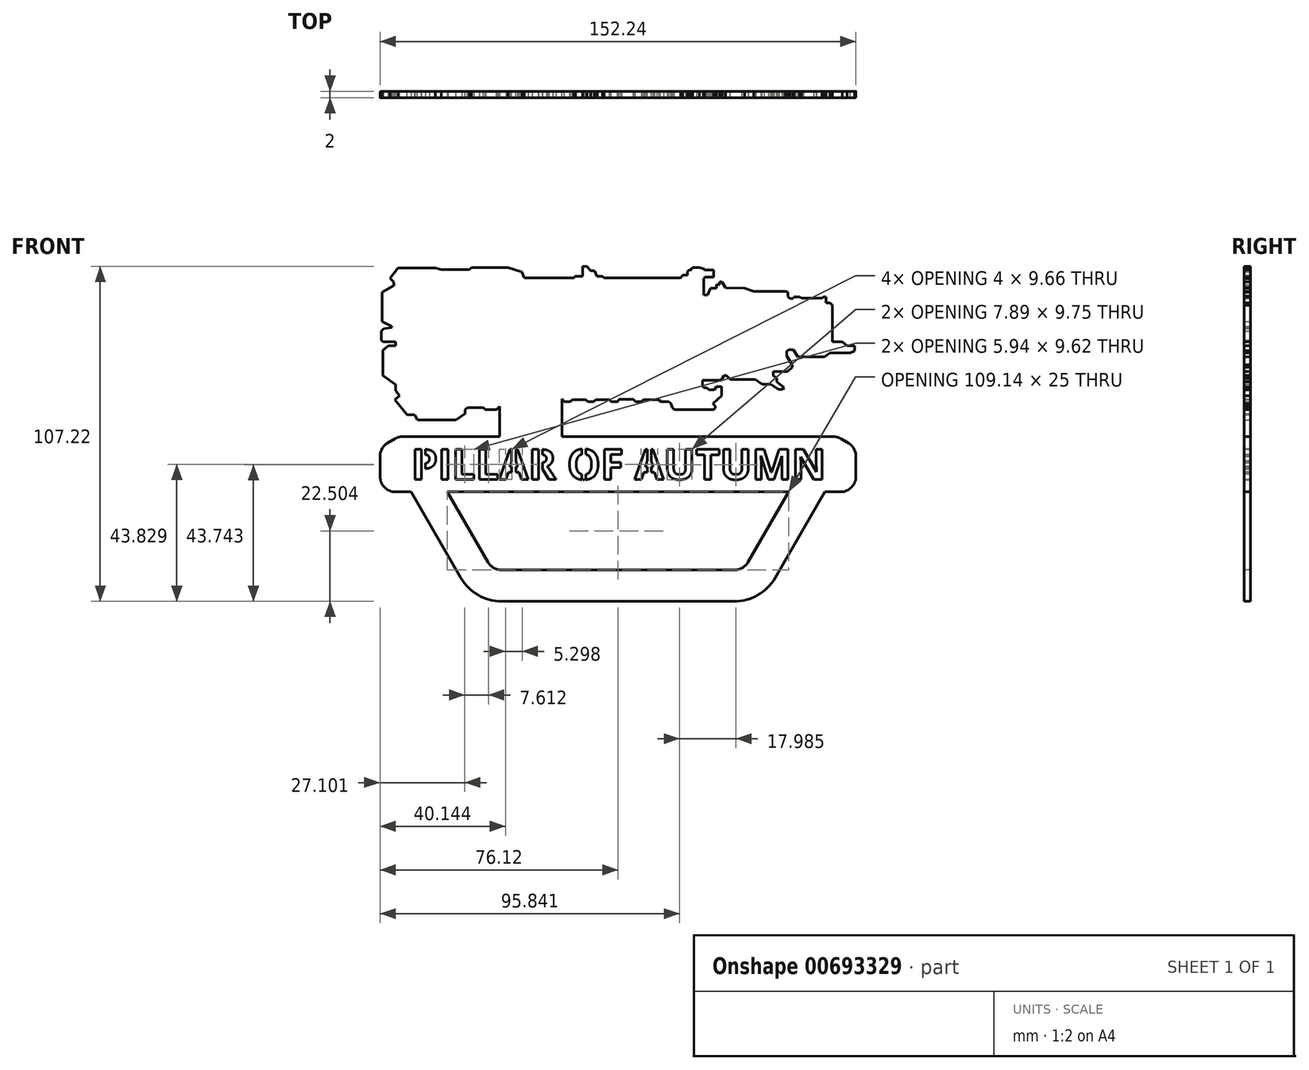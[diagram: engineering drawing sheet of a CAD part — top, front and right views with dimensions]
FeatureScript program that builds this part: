
annotation { "Feature Type Name" : "Feature", "Feature Type Description" : "" }
export const myFeature = defineFeature(function(context is Context, id is Id, definition is map)
    precondition{}
    {
        {
            var Q0;
            Q0=qCreatedBy(makeId("Front.planeOp"),FACE);
            var sketch = newSketch(context, id + "F0", { "sketchPlane" : qUnion([Q0])});
            skLineSegment(sketch, "E0", {"start": v(-54.7, 20.46) * mm, "end": v(-44.83, 20.46) * mm});
            skLineSegment(sketch, "E1", {"start": v(-44.83, 20.46) * mm, "end": v(-43.33, 20.02) * mm});
            skLineSegment(sketch, "E2", {"start": v(-43.33, 20.02) * mm, "end": v(-35.89, 20.02) * mm});
            skLineSegment(sketch, "E3", {"start": v(-35.89, 20.02) * mm, "end": v(-35.36, 20.5) * mm});
            skLineSegment(sketch, "E4", {"start": v(-35.36, 20.5) * mm, "end": v(-25.77, 20.5) * mm});
            skLineSegment(sketch, "E5", {"start": v(-25.77, 20.5) * mm, "end": v(-22.18, 19.35) * mm});
            skLineSegment(sketch, "E6", {"start": v(-22.18, 19.35) * mm, "end": v(-21.5, 17.82) * mm});
            skLineSegment(sketch, "E7", {"start": v(-21.5, 17.82) * mm, "end": v(-8.55, 17.82) * mm});
            skLineSegment(sketch, "E8", {"start": v(-8.55, 17.82) * mm, "end": v(-8.23, 18.3) * mm});
            skLineSegment(sketch, "E9", {"start": v(-8.23, 18.3) * mm, "end": v(-6.22, 18.3) * mm});
            skLineSegment(sketch, "E10", {"start": v(-6.22, 18.3) * mm, "end": v(-6.22, 20.89) * mm});
            skLineSegment(sketch, "E11", {"start": v(-6.22, 20.89) * mm, "end": v(-5.15, 20.89) * mm});
            skLineSegment(sketch, "E12", {"start": v(-5.15, 20.89) * mm, "end": v(-4.2, 19.76) * mm});
            skLineSegment(sketch, "E13", {"start": v(-4.2, 19.76) * mm, "end": v(-3.13, 19.76) * mm});
            skLineSegment(sketch, "E14", {"start": v(-3.13, 19.76) * mm, "end": v(-2.5, 18.3) * mm});
            skLineSegment(sketch, "E15", {"start": v(-2.5, 18.3) * mm, "end": v(-1.08, 18.3) * mm});
            skLineSegment(sketch, "E16", {"start": v(-1.08, 18.3) * mm, "end": v(-0.64, 17.82) * mm});
            skLineSegment(sketch, "E17", {"start": v(-0.64, 17.82) * mm, "end": v(19.49, 17.82) * mm});
            skLineSegment(sketch, "E18", {"start": v(19.49, 17.82) * mm, "end": v(19.98, 18.57) * mm});
            skLineSegment(sketch, "E19", {"start": v(19.98, 18.57) * mm, "end": v(21.22, 18.57) * mm});
            skLineSegment(sketch, "E20", {"start": v(21.22, 18.57) * mm, "end": v(21.22, 19.5) * mm});
            skLineSegment(sketch, "E21", {"start": v(21.22, 19.5) * mm, "end": v(21.62, 19.92) * mm});
            skLineSegment(sketch, "E22", {"start": v(21.62, 19.92) * mm, "end": v(22.31, 19.92) * mm});
            skLineSegment(sketch, "E23", {"start": v(22.31, 19.92) * mm, "end": v(22.31, 20.34) * mm});
            skLineSegment(sketch, "E24", {"start": v(22.31, 20.34) * mm, "end": v(22.56, 20.59) * mm});
            skLineSegment(sketch, "E25", {"start": v(22.56, 20.59) * mm, "end": v(24.39, 20.59) * mm});
            skLineSegment(sketch, "E26", {"start": v(24.39, 20.59) * mm, "end": v(25.46, 20.2) * mm});
            skLineSegment(sketch, "E27", {"start": v(25.46, 20.2) * mm, "end": v(25.7, 19.92) * mm});
            skLineSegment(sketch, "E28", {"start": v(25.7, 19.92) * mm, "end": v(28.13, 19.92) * mm});
            skLineSegment(sketch, "E29", {"start": v(28.13, 19.92) * mm, "end": v(28.13, 18.01) * mm});
            skLineSegment(sketch, "E30", {"start": v(28.13, 18.01) * mm, "end": v(25.76, 18.01) * mm});
            skLineSegment(sketch, "E31", {"start": v(25.76, 18.01) * mm, "end": v(25.46, 17.63) * mm});
            skLineSegment(sketch, "E32", {"start": v(25.46, 17.63) * mm, "end": v(25.46, 13.38) * mm});
            skLineSegment(sketch, "E33", {"start": v(25.46, 13.38) * mm, "end": v(26.57, 13.38) * mm});
            skLineSegment(sketch, "E34", {"start": v(26.57, 13.38) * mm, "end": v(27.23, 15.17) * mm});
            skLineSegment(sketch, "E35", {"start": v(27.23, 15.17) * mm, "end": v(28.85, 15.17) * mm});
            skLineSegment(sketch, "E36", {"start": v(28.85, 15.17) * mm, "end": v(28.85, 16.09) * mm});
            skLineSegment(sketch, "E37", {"start": v(28.85, 16.09) * mm, "end": v(29.71, 16.09) * mm});
            skLineSegment(sketch, "E38", {"start": v(29.71, 16.09) * mm, "end": v(29.71, 16.78) * mm});
            skLineSegment(sketch, "E39", {"start": v(29.71, 16.78) * mm, "end": v(30.29, 16.78) * mm});
            skLineSegment(sketch, "E40", {"start": v(30.29, 16.78) * mm, "end": v(31.21, 15.2) * mm});
            skLineSegment(sketch, "E41", {"start": v(31.21, 15.2) * mm, "end": v(36.22, 15.17) * mm});
            skLineSegment(sketch, "E42", {"start": v(36.22, 15.17) * mm, "end": v(38.62, 14.3) * mm});
            skLineSegment(sketch, "E43", {"start": v(38.62, 14.3) * mm, "end": v(46.94, 14.3) * mm});
            skLineSegment(sketch, "E44", {"start": v(46.94, 14.3) * mm, "end": v(47.62, 14.06) * mm});
            skLineSegment(sketch, "E45", {"start": v(47.62, 14.06) * mm, "end": v(47.62, 13) * mm});
            skLineSegment(sketch, "E46", {"start": v(47.62, 13) * mm, "end": v(48.07, 12.38) * mm});
            skLineSegment(sketch, "E47", {"start": v(48.07, 12.38) * mm, "end": v(48.92, 12.38) * mm});
            skLineSegment(sketch, "E48", {"start": v(48.92, 12.38) * mm, "end": v(49.1, 12.88) * mm});
            skLineSegment(sketch, "E49", {"start": v(49.1, 12.88) * mm, "end": v(50.74, 12.88) * mm});
            skLineSegment(sketch, "E50", {"start": v(50.74, 12.88) * mm, "end": v(51.11, 12.5) * mm});
            skLineSegment(sketch, "E51", {"start": v(51.11, 12.5) * mm, "end": v(56.53, 12.5) * mm});
            skLineSegment(sketch, "E52", {"start": v(56.53, 12.5) * mm, "end": v(56.87, 12.88) * mm});
            skLineSegment(sketch, "E53", {"start": v(56.87, 12.88) * mm, "end": v(57.58, 12.88) * mm});
            skLineSegment(sketch, "E54", {"start": v(57.58, 12.88) * mm, "end": v(57.58, 11.32) * mm});
            skLineSegment(sketch, "E55", {"start": v(57.58, 11.32) * mm, "end": v(58.55, 11.32) * mm});
            skLineSegment(sketch, "E56", {"start": v(58.55, 11.32) * mm, "end": v(59.24, 10.67) * mm});
            skLineSegment(sketch, "E57", {"start": v(59.24, 10.67) * mm, "end": v(59.24, 1.08) * mm});
            skLineSegment(sketch, "E58", {"start": v(59.24, 1.08) * mm, "end": v(61.8, 1.08) * mm});
            skLineSegment(sketch, "E59", {"start": v(61.8, 1.08) * mm, "end": v(63.08, 0) * mm});
            skLineSegment(sketch, "E60", {"start": v(63.08, 0) * mm, "end": v(65.04, 0) * mm});
            skLineSegment(sketch, "E61", {"start": v(65.04, 0) * mm, "end": v(65.04, -1.34) * mm});
            skLineSegment(sketch, "E62", {"start": v(65.04, -1.34) * mm, "end": v(63.94, -1.8) * mm});
            skLineSegment(sketch, "E63", {"start": v(63.94, -1.8) * mm, "end": v(58.55, -1.8) * mm});
            skLineSegment(sketch, "E64", {"start": v(58.55, -1.8) * mm, "end": v(57.14, -2.9) * mm});
            skLineSegment(sketch, "E65", {"start": v(57.14, -2.9) * mm, "end": v(50.16, -2.9) * mm});
            skLineSegment(sketch, "E66", {"start": v(50.16, -2.9) * mm, "end": v(49.07, -1.06) * mm});
            skLineSegment(sketch, "E67", {"start": v(49.07, -1.06) * mm, "end": v(47.74, -1.06) * mm});
            skLineSegment(sketch, "E68", {"start": v(47.74, -1.06) * mm, "end": v(47.27, -1.4) * mm});
            skLineSegment(sketch, "E69", {"start": v(47.27, -1.4) * mm, "end": v(47.27, -2.63) * mm});
            skLineSegment(sketch, "E70", {"start": v(47.27, -2.63) * mm, "end": v(48.68, -5) * mm});
            skLineSegment(sketch, "E71", {"start": v(48.68, -5) * mm, "end": v(48.68, -5.57) * mm});
            skLineSegment(sketch, "E72", {"start": v(48.68, -5.57) * mm, "end": v(47.41, -6.74) * mm});
            skLineSegment(sketch, "E73", {"start": v(47.41, -6.74) * mm, "end": v(43.7, -6.74) * mm});
            skLineSegment(sketch, "E74", {"start": v(43.7, -6.74) * mm, "end": v(43.7, -7.74) * mm});
            skLineSegment(sketch, "E75", {"start": v(43.7, -7.74) * mm, "end": v(44.62, -8.55) * mm});
            skLineSegment(sketch, "E76", {"start": v(44.62, -8.55) * mm, "end": v(44.62, -9.42) * mm});
            skLineSegment(sketch, "E77", {"start": v(44.62, -9.42) * mm, "end": v(46.58, -10.94) * mm});
            skLineSegment(sketch, "E78", {"start": v(46.58, -10.94) * mm, "end": v(46.23, -11.38) * mm});
            skLineSegment(sketch, "E79", {"start": v(46.23, -11.38) * mm, "end": v(45.04, -11.38) * mm});
            skLineSegment(sketch, "E80", {"start": v(45.04, -11.38) * mm, "end": v(43.12, -10.02) * mm});
            skLineSegment(sketch, "E81", {"start": v(43.12, -10.02) * mm, "end": v(40.82, -10.02) * mm});
            skLineSegment(sketch, "E82", {"start": v(40.82, -10.02) * mm, "end": v(39.07, -8.83) * mm});
            skLineSegment(sketch, "E83", {"start": v(39.07, -8.83) * mm, "end": v(32.52, -8.83) * mm});
            skLineSegment(sketch, "E84", {"start": v(32.52, -8.83) * mm, "end": v(31.4, -7.8) * mm});
            skLineSegment(sketch, "E85", {"start": v(31.4, -7.8) * mm, "end": v(30.76, -7.8) * mm});
            skLineSegment(sketch, "E86", {"start": v(30.76, -7.8) * mm, "end": v(30.06, -9.02) * mm});
            skLineSegment(sketch, "E87", {"start": v(30.06, -9.02) * mm, "end": v(25.2, -9.02) * mm});
            skLineSegment(sketch, "E88", {"start": v(25.2, -9.02) * mm, "end": v(25.2, -10.62) * mm});
            skLineSegment(sketch, "E89", {"start": v(25.2, -10.62) * mm, "end": v(25.6, -11.03) * mm});
            skLineSegment(sketch, "E90", {"start": v(25.6, -11.03) * mm, "end": v(26.3, -11.03) * mm});
            skLineSegment(sketch, "E91", {"start": v(26.3, -11.03) * mm, "end": v(26.81, -11.57) * mm});
            skLineSegment(sketch, "E92", {"start": v(26.81, -11.57) * mm, "end": v(28.34, -11.57) * mm});
            skLineSegment(sketch, "E93", {"start": v(28.34, -11.57) * mm, "end": v(28.87, -10.67) * mm});
            skLineSegment(sketch, "E94", {"start": v(28.87, -10.67) * mm, "end": v(30.18, -10.67) * mm});
            skLineSegment(sketch, "E95", {"start": v(30.18, -10.67) * mm, "end": v(30.18, -13.07) * mm});
            skLineSegment(sketch, "E96", {"start": v(30.18, -13.07) * mm, "end": v(27.93, -15.14) * mm});
            skLineSegment(sketch, "E97", {"start": v(27.93, -15.14) * mm, "end": v(28.48, -15.74) * mm});
            skLineSegment(sketch, "E98", {"start": v(28.48, -15.74) * mm, "end": v(28.48, -16.3) * mm});
            skLineSegment(sketch, "E99", {"start": v(28.48, -16.3) * mm, "end": v(28.11, -16.7) * mm});
            skLineSegment(sketch, "E100", {"start": v(28.11, -16.7) * mm, "end": v(17.79, -16.7) * mm});
            skLineSegment(sketch, "E101", {"start": v(17.79, -16.7) * mm, "end": v(17.26, -16.2) * mm});
            skLineSegment(sketch, "E102", {"start": v(17.26, -16.2) * mm, "end": v(16.82, -15.01) * mm});
            skLineSegment(sketch, "E103", {"start": v(16.82, -15.01) * mm, "end": v(16.34, -14.6) * mm});
            skLineSegment(sketch, "E104", {"start": v(16.34, -14.6) * mm, "end": v(14.18, -14.67) * mm});
            skLineSegment(sketch, "E105", {"start": v(14.18, -14.67) * mm, "end": v(13.8, -14.17) * mm});
            skLineSegment(sketch, "E106", {"start": v(13.8, -14.17) * mm, "end": v(9.68, -14.17) * mm});
            skLineSegment(sketch, "E107", {"start": v(9.68, -14.17) * mm, "end": v(9.26, -14.68) * mm});
            skLineSegment(sketch, "E108", {"start": v(9.26, -14.68) * mm, "end": v(7.64, -14.68) * mm});
            skLineSegment(sketch, "E109", {"start": v(7.64, -14.68) * mm, "end": v(7.1, -14.07) * mm});
            skLineSegment(sketch, "E110", {"start": v(7.1, -14.07) * mm, "end": v(3.34, -14.07) * mm});
            skLineSegment(sketch, "E111", {"start": v(3.34, -14.07) * mm, "end": v(2.95, -14.65) * mm});
            skLineSegment(sketch, "E112", {"start": v(2.95, -14.65) * mm, "end": v(1.26, -14.65) * mm});
            skLineSegment(sketch, "E113", {"start": v(1.26, -14.65) * mm, "end": v(0.83, -14.1) * mm});
            skLineSegment(sketch, "E114", {"start": v(0.83, -14.1) * mm, "end": v(-2.8, -14.1) * mm});
            skLineSegment(sketch, "E115", {"start": v(-2.8, -14.1) * mm, "end": v(-3.29, -14.65) * mm});
            skLineSegment(sketch, "E116", {"start": v(-3.29, -14.65) * mm, "end": v(-4.88, -14.65) * mm});
            skLineSegment(sketch, "E117", {"start": v(-4.88, -14.65) * mm, "end": v(-5.47, -14.11) * mm});
            skLineSegment(sketch, "E118", {"start": v(-5.47, -14.11) * mm, "end": v(-9, -14.11) * mm});
            skLineSegment(sketch, "E119", {"start": v(-9, -14.11) * mm, "end": v(-9.5, -14.65) * mm});
            skLineSegment(sketch, "E120", {"start": v(-9.5, -14.65) * mm, "end": v(-11.05, -14.65) * mm});
            skLineSegment(sketch, "E121", {"start": v(-11.05, -14.65) * mm, "end": v(-11.63, -13.96) * mm});
            skLineSegment(sketch, "E122", {"start": v(-11.63, -13.96) * mm, "end": v(-14.05, -13.96) * mm});
            skLineSegment(sketch, "E123", {"start": v(-14.05, -13.96) * mm, "end": v(-16.32, -16.2) * mm});
            skLineSegment(sketch, "E124", {"start": v(-16.32, -16.2) * mm, "end": v(-25.86, -16.2) * mm});
            skLineSegment(sketch, "E125", {"start": v(-25.86, -16.2) * mm, "end": v(-26.54, -15.2) * mm});
            skLineSegment(sketch, "E126", {"start": v(-26.54, -15.2) * mm, "end": v(-27.3, -15.2) * mm});
            skLineSegment(sketch, "E127", {"start": v(-27.3, -15.2) * mm, "end": v(-28.87, -16.7) * mm});
            skLineSegment(sketch, "E128", {"start": v(-28.87, -16.7) * mm, "end": v(-31.79, -16.7) * mm});
            skLineSegment(sketch, "E129", {"start": v(-31.79, -16.7) * mm, "end": v(-32.27, -16.2) * mm});
            skLineSegment(sketch, "E130", {"start": v(-32.27, -16.2) * mm, "end": v(-36.4, -16.2) * mm});
            skLineSegment(sketch, "E131", {"start": v(-36.4, -16.2) * mm, "end": v(-37.06, -16.7) * mm});
            skLineSegment(sketch, "E132", {"start": v(-37.06, -16.7) * mm, "end": v(-37.06, -17.8) * mm});
            skLineSegment(sketch, "E133", {"start": v(-37.06, -17.8) * mm, "end": v(-39.5, -19.41) * mm});
            skLineSegment(sketch, "E134", {"start": v(-39.5, -19.41) * mm, "end": v(-49.57, -19.41) * mm});
            skLineSegment(sketch, "E135", {"start": v(-49.57, -19.41) * mm, "end": v(-50.32, -18.05) * mm});
            skLineSegment(sketch, "E136", {"start": v(-50.32, -18.05) * mm, "end": v(-52.28, -18.05) * mm});
            skLineSegment(sketch, "E137", {"start": v(-52.28, -18.05) * mm, "end": v(-55.5, -14.11) * mm});
            skLineSegment(sketch, "E138", {"start": v(-55.5, -14.11) * mm, "end": v(-54.23, -13.06) * mm});
            skLineSegment(sketch, "E139", {"start": v(-54.23, -13.06) * mm, "end": v(-55.3, -11.76) * mm});
            skLineSegment(sketch, "E140", {"start": v(-55.3, -11.76) * mm, "end": v(-55.3, -10.21) * mm});
            skLineSegment(sketch, "E141", {"start": v(-55.3, -10.21) * mm, "end": v(-58.58, -7.82) * mm});
            skLineSegment(sketch, "E142", {"start": v(-58.58, -7.82) * mm, "end": v(-58.58, -1.1) * mm});
            skLineSegment(sketch, "E143", {"start": v(-58.58, -1.1) * mm, "end": v(-57.2, 0) * mm});
            skLineSegment(sketch, "E144", {"start": v(-57.2, 0) * mm, "end": v(-55.3, 0) * mm});
            skLineSegment(sketch, "E145", {"start": v(-55.3, 0) * mm, "end": v(-55.3, 1.1) * mm});
            skLineSegment(sketch, "E146", {"start": v(-55.3, 1.1) * mm, "end": v(-58.58, 1.1) * mm});
            skLineSegment(sketch, "E147", {"start": v(-58.58, 1.1) * mm, "end": v(-59, 1.53) * mm});
            skLineSegment(sketch, "E148", {"start": v(-59, 1.53) * mm, "end": v(-59, 3.87) * mm});
            skLineSegment(sketch, "E149", {"start": v(-59, 3.87) * mm, "end": v(-58.42, 4.53) * mm});
            skLineSegment(sketch, "E150", {"start": v(-58.42, 4.53) * mm, "end": v(-56.24, 4.83) * mm});
            skLineSegment(sketch, "E151", {"start": v(-56.24, 4.83) * mm, "end": v(-56.28, 5.09) * mm});
            skLineSegment(sketch, "E152", {"start": v(-56.28, 5.09) * mm, "end": v(-58.86, 6.39) * mm});
            skLineSegment(sketch, "E153", {"start": v(-58.86, 6.39) * mm, "end": v(-58.86, 14.13) * mm});
            skLineSegment(sketch, "E154", {"start": v(-58.86, 14.13) * mm, "end": v(-55.69, 15.85) * mm});
            skLineSegment(sketch, "E155", {"start": v(-55.69, 15.85) * mm, "end": v(-55.81, 16.76) * mm});
            skLineSegment(sketch, "E156", {"start": v(-55.81, 16.76) * mm, "end": v(-56.75, 17.77) * mm});
            skLineSegment(sketch, "E157", {"start": v(-56.75, 17.77) * mm, "end": v(-54.7, 20.46) * mm});
            skSolve(sketch);
        }
        {
            var Q0;
            Q0 = qSketchRegion(id + "F0", true);
            extrude(context, id + "F1", {"entities" : qUnion([Q0]), "depth" : 2 * mm, "offsetDistance" : 25 * mm});
        }
        {
            var Q0;
            Q0=makeQuery(id+"F1.opExtrude","SWEPT_BODY",BODY,{"disambiguationData":[OSD([sQuery(id+"F0.wireOp",EDGE,"E0"),sQuery(id+"F0.wireOp",EDGE,"E1"),sQuery(id+"F0.wireOp",EDGE,"E2"),sQuery(id+"F0.wireOp",EDGE,"E3"),sQuery(id+"F0.wireOp",EDGE,"E4"),sQuery(id+"F0.wireOp",EDGE,"E5"),sQuery(id+"F0.wireOp",EDGE,"E6"),sQuery(id+"F0.wireOp",EDGE,"E7"),sQuery(id+"F0.wireOp",EDGE,"E8"),sQuery(id+"F0.wireOp",EDGE,"E9"),sQuery(id+"F0.wireOp",EDGE,"E10"),sQuery(id+"F0.wireOp",EDGE,"E11"),sQuery(id+"F0.wireOp",EDGE,"E12"),sQuery(id+"F0.wireOp",EDGE,"E13"),sQuery(id+"F0.wireOp",EDGE,"E14"),sQuery(id+"F0.wireOp",EDGE,"E15"),sQuery(id+"F0.wireOp",EDGE,"E16"),sQuery(id+"F0.wireOp",EDGE,"E17"),sQuery(id+"F0.wireOp",EDGE,"E18"),sQuery(id+"F0.wireOp",EDGE,"E19"),sQuery(id+"F0.wireOp",EDGE,"E20"),sQuery(id+"F0.wireOp",EDGE,"E21"),sQuery(id+"F0.wireOp",EDGE,"E22"),sQuery(id+"F0.wireOp",EDGE,"E23"),sQuery(id+"F0.wireOp",EDGE,"E24"),sQuery(id+"F0.wireOp",EDGE,"E25"),sQuery(id+"F0.wireOp",EDGE,"E26"),sQuery(id+"F0.wireOp",EDGE,"E27"),sQuery(id+"F0.wireOp",EDGE,"E28"),sQuery(id+"F0.wireOp",EDGE,"E29"),sQuery(id+"F0.wireOp",EDGE,"E30"),sQuery(id+"F0.wireOp",EDGE,"E31"),sQuery(id+"F0.wireOp",EDGE,"E32"),sQuery(id+"F0.wireOp",EDGE,"E33"),sQuery(id+"F0.wireOp",EDGE,"E34"),sQuery(id+"F0.wireOp",EDGE,"E35"),sQuery(id+"F0.wireOp",EDGE,"E36"),sQuery(id+"F0.wireOp",EDGE,"E37"),sQuery(id+"F0.wireOp",EDGE,"E38"),sQuery(id+"F0.wireOp",EDGE,"E39"),sQuery(id+"F0.wireOp",EDGE,"E40"),sQuery(id+"F0.wireOp",EDGE,"E41"),sQuery(id+"F0.wireOp",EDGE,"E42"),sQuery(id+"F0.wireOp",EDGE,"E43"),sQuery(id+"F0.wireOp",EDGE,"E44"),sQuery(id+"F0.wireOp",EDGE,"E45"),sQuery(id+"F0.wireOp",EDGE,"E46"),sQuery(id+"F0.wireOp",EDGE,"E47"),sQuery(id+"F0.wireOp",EDGE,"E48"),sQuery(id+"F0.wireOp",EDGE,"E49"),sQuery(id+"F0.wireOp",EDGE,"E50"),sQuery(id+"F0.wireOp",EDGE,"E51"),sQuery(id+"F0.wireOp",EDGE,"E52"),sQuery(id+"F0.wireOp",EDGE,"E53"),sQuery(id+"F0.wireOp",EDGE,"E54"),sQuery(id+"F0.wireOp",EDGE,"E55"),sQuery(id+"F0.wireOp",EDGE,"E56"),sQuery(id+"F0.wireOp",EDGE,"E57"),sQuery(id+"F0.wireOp",EDGE,"E58"),sQuery(id+"F0.wireOp",EDGE,"E59"),sQuery(id+"F0.wireOp",EDGE,"E60"),sQuery(id+"F0.wireOp",EDGE,"E61"),sQuery(id+"F0.wireOp",EDGE,"E62"),sQuery(id+"F0.wireOp",EDGE,"E63"),sQuery(id+"F0.wireOp",EDGE,"E64"),sQuery(id+"F0.wireOp",EDGE,"E65"),sQuery(id+"F0.wireOp",EDGE,"E66"),sQuery(id+"F0.wireOp",EDGE,"E67"),sQuery(id+"F0.wireOp",EDGE,"E68"),sQuery(id+"F0.wireOp",EDGE,"E69"),sQuery(id+"F0.wireOp",EDGE,"E70"),sQuery(id+"F0.wireOp",EDGE,"E71"),sQuery(id+"F0.wireOp",EDGE,"E72"),sQuery(id+"F0.wireOp",EDGE,"E73"),sQuery(id+"F0.wireOp",EDGE,"E74"),sQuery(id+"F0.wireOp",EDGE,"E75"),sQuery(id+"F0.wireOp",EDGE,"E76"),sQuery(id+"F0.wireOp",EDGE,"E77"),sQuery(id+"F0.wireOp",EDGE,"E78"),sQuery(id+"F0.wireOp",EDGE,"E79"),sQuery(id+"F0.wireOp",EDGE,"E80"),sQuery(id+"F0.wireOp",EDGE,"E81"),sQuery(id+"F0.wireOp",EDGE,"E82"),sQuery(id+"F0.wireOp",EDGE,"E83"),sQuery(id+"F0.wireOp",EDGE,"E84"),sQuery(id+"F0.wireOp",EDGE,"E85"),sQuery(id+"F0.wireOp",EDGE,"E86"),sQuery(id+"F0.wireOp",EDGE,"E87"),sQuery(id+"F0.wireOp",EDGE,"E88"),sQuery(id+"F0.wireOp",EDGE,"E89"),sQuery(id+"F0.wireOp",EDGE,"E90"),sQuery(id+"F0.wireOp",EDGE,"E91"),sQuery(id+"F0.wireOp",EDGE,"E92"),sQuery(id+"F0.wireOp",EDGE,"E93"),sQuery(id+"F0.wireOp",EDGE,"E94"),sQuery(id+"F0.wireOp",EDGE,"E95"),sQuery(id+"F0.wireOp",EDGE,"E96"),sQuery(id+"F0.wireOp",EDGE,"E97"),sQuery(id+"F0.wireOp",EDGE,"E98"),sQuery(id+"F0.wireOp",EDGE,"E99"),sQuery(id+"F0.wireOp",EDGE,"E100"),sQuery(id+"F0.wireOp",EDGE,"E101"),sQuery(id+"F0.wireOp",EDGE,"E102"),sQuery(id+"F0.wireOp",EDGE,"E103"),sQuery(id+"F0.wireOp",EDGE,"E104"),sQuery(id+"F0.wireOp",EDGE,"E105"),sQuery(id+"F0.wireOp",EDGE,"E106"),sQuery(id+"F0.wireOp",EDGE,"E107"),sQuery(id+"F0.wireOp",EDGE,"E108"),sQuery(id+"F0.wireOp",EDGE,"E109"),sQuery(id+"F0.wireOp",EDGE,"E110"),sQuery(id+"F0.wireOp",EDGE,"E111"),sQuery(id+"F0.wireOp",EDGE,"E112"),sQuery(id+"F0.wireOp",EDGE,"E113"),sQuery(id+"F0.wireOp",EDGE,"E114"),sQuery(id+"F0.wireOp",EDGE,"E115"),sQuery(id+"F0.wireOp",EDGE,"E116"),sQuery(id+"F0.wireOp",EDGE,"E117"),sQuery(id+"F0.wireOp",EDGE,"E118"),sQuery(id+"F0.wireOp",EDGE,"E119"),sQuery(id+"F0.wireOp",EDGE,"E120"),sQuery(id+"F0.wireOp",EDGE,"E121"),sQuery(id+"F0.wireOp",EDGE,"E122"),sQuery(id+"F0.wireOp",EDGE,"E123"),sQuery(id+"F0.wireOp",EDGE,"E124"),sQuery(id+"F0.wireOp",EDGE,"E125"),sQuery(id+"F0.wireOp",EDGE,"E126"),sQuery(id+"F0.wireOp",EDGE,"E127"),sQuery(id+"F0.wireOp",EDGE,"E128"),sQuery(id+"F0.wireOp",EDGE,"E129"),sQuery(id+"F0.wireOp",EDGE,"E130"),sQuery(id+"F0.wireOp",EDGE,"E131"),sQuery(id+"F0.wireOp",EDGE,"E132"),sQuery(id+"F0.wireOp",EDGE,"E133"),sQuery(id+"F0.wireOp",EDGE,"E134"),sQuery(id+"F0.wireOp",EDGE,"E135"),sQuery(id+"F0.wireOp",EDGE,"E136"),sQuery(id+"F0.wireOp",EDGE,"E137"),sQuery(id+"F0.wireOp",EDGE,"E138"),sQuery(id+"F0.wireOp",EDGE,"E139"),sQuery(id+"F0.wireOp",EDGE,"E140"),sQuery(id+"F0.wireOp",EDGE,"E141"),sQuery(id+"F0.wireOp",EDGE,"E142"),sQuery(id+"F0.wireOp",EDGE,"E143"),sQuery(id+"F0.wireOp",EDGE,"E144"),sQuery(id+"F0.wireOp",EDGE,"E145"),sQuery(id+"F0.wireOp",EDGE,"E146"),sQuery(id+"F0.wireOp",EDGE,"E147"),sQuery(id+"F0.wireOp",EDGE,"E148"),sQuery(id+"F0.wireOp",EDGE,"E149"),sQuery(id+"F0.wireOp",EDGE,"E150"),sQuery(id+"F0.wireOp",EDGE,"E151"),sQuery(id+"F0.wireOp",EDGE,"E152"),sQuery(id+"F0.wireOp",EDGE,"E153"),sQuery(id+"F0.wireOp",EDGE,"E154"),sQuery(id+"F0.wireOp",EDGE,"E155"),sQuery(id+"F0.wireOp",EDGE,"E156"),sQuery(id+"F0.wireOp",EDGE,"E157")])]});
            var Q1;
            Q1=makeQuery(id+"F1.opExtrude","CAP_VERTEX",VERTEX,{"disambiguationData":[OSD([sQuery(id+"F0.wireOp",EDGE,"E145"),sQuery(id+"F0.wireOp",EDGE,"E146")])],"isStart":false});
            transform(context, id + "F2", {"entities" : qUnion([Q0]), "transformType" : TransformType.SCALE_UNIFORMLY, "scale" : 1.22, "scalePoint" : qUnion([Q1]), "makeCopy" : false});
        }
        {
            var Q0;
            Q0=makeQuery(id+"F1.opExtrude","CAP_FACE",FACE,{"disambiguationData":[OSD([sQuery(id+"F0.wireOp",EDGE,"E0"),sQuery(id+"F0.wireOp",EDGE,"E1"),sQuery(id+"F0.wireOp",EDGE,"E2"),sQuery(id+"F0.wireOp",EDGE,"E3"),sQuery(id+"F0.wireOp",EDGE,"E4"),sQuery(id+"F0.wireOp",EDGE,"E5"),sQuery(id+"F0.wireOp",EDGE,"E6"),sQuery(id+"F0.wireOp",EDGE,"E7"),sQuery(id+"F0.wireOp",EDGE,"E8"),sQuery(id+"F0.wireOp",EDGE,"E9"),sQuery(id+"F0.wireOp",EDGE,"E10"),sQuery(id+"F0.wireOp",EDGE,"E11"),sQuery(id+"F0.wireOp",EDGE,"E12"),sQuery(id+"F0.wireOp",EDGE,"E13"),sQuery(id+"F0.wireOp",EDGE,"E14"),sQuery(id+"F0.wireOp",EDGE,"E15"),sQuery(id+"F0.wireOp",EDGE,"E16"),sQuery(id+"F0.wireOp",EDGE,"E17"),sQuery(id+"F0.wireOp",EDGE,"E18"),sQuery(id+"F0.wireOp",EDGE,"E19"),sQuery(id+"F0.wireOp",EDGE,"E20"),sQuery(id+"F0.wireOp",EDGE,"E21"),sQuery(id+"F0.wireOp",EDGE,"E22"),sQuery(id+"F0.wireOp",EDGE,"E23"),sQuery(id+"F0.wireOp",EDGE,"E24"),sQuery(id+"F0.wireOp",EDGE,"E25"),sQuery(id+"F0.wireOp",EDGE,"E26"),sQuery(id+"F0.wireOp",EDGE,"E27"),sQuery(id+"F0.wireOp",EDGE,"E28"),sQuery(id+"F0.wireOp",EDGE,"E29"),sQuery(id+"F0.wireOp",EDGE,"E30"),sQuery(id+"F0.wireOp",EDGE,"E31"),sQuery(id+"F0.wireOp",EDGE,"E32"),sQuery(id+"F0.wireOp",EDGE,"E33"),sQuery(id+"F0.wireOp",EDGE,"E34"),sQuery(id+"F0.wireOp",EDGE,"E35"),sQuery(id+"F0.wireOp",EDGE,"E36"),sQuery(id+"F0.wireOp",EDGE,"E37"),sQuery(id+"F0.wireOp",EDGE,"E38"),sQuery(id+"F0.wireOp",EDGE,"E39"),sQuery(id+"F0.wireOp",EDGE,"E40"),sQuery(id+"F0.wireOp",EDGE,"E41"),sQuery(id+"F0.wireOp",EDGE,"E42"),sQuery(id+"F0.wireOp",EDGE,"E43"),sQuery(id+"F0.wireOp",EDGE,"E44"),sQuery(id+"F0.wireOp",EDGE,"E45"),sQuery(id+"F0.wireOp",EDGE,"E46"),sQuery(id+"F0.wireOp",EDGE,"E47"),sQuery(id+"F0.wireOp",EDGE,"E48"),sQuery(id+"F0.wireOp",EDGE,"E49"),sQuery(id+"F0.wireOp",EDGE,"E50"),sQuery(id+"F0.wireOp",EDGE,"E51"),sQuery(id+"F0.wireOp",EDGE,"E52"),sQuery(id+"F0.wireOp",EDGE,"E53"),sQuery(id+"F0.wireOp",EDGE,"E54"),sQuery(id+"F0.wireOp",EDGE,"E55"),sQuery(id+"F0.wireOp",EDGE,"E56"),sQuery(id+"F0.wireOp",EDGE,"E57"),sQuery(id+"F0.wireOp",EDGE,"E58"),sQuery(id+"F0.wireOp",EDGE,"E59"),sQuery(id+"F0.wireOp",EDGE,"E60"),sQuery(id+"F0.wireOp",EDGE,"E61"),sQuery(id+"F0.wireOp",EDGE,"E62"),sQuery(id+"F0.wireOp",EDGE,"E63"),sQuery(id+"F0.wireOp",EDGE,"E64"),sQuery(id+"F0.wireOp",EDGE,"E65"),sQuery(id+"F0.wireOp",EDGE,"E66"),sQuery(id+"F0.wireOp",EDGE,"E67"),sQuery(id+"F0.wireOp",EDGE,"E68"),sQuery(id+"F0.wireOp",EDGE,"E69"),sQuery(id+"F0.wireOp",EDGE,"E70"),sQuery(id+"F0.wireOp",EDGE,"E71"),sQuery(id+"F0.wireOp",EDGE,"E72"),sQuery(id+"F0.wireOp",EDGE,"E73"),sQuery(id+"F0.wireOp",EDGE,"E74"),sQuery(id+"F0.wireOp",EDGE,"E75"),sQuery(id+"F0.wireOp",EDGE,"E76"),sQuery(id+"F0.wireOp",EDGE,"E77"),sQuery(id+"F0.wireOp",EDGE,"E78"),sQuery(id+"F0.wireOp",EDGE,"E79"),sQuery(id+"F0.wireOp",EDGE,"E80"),sQuery(id+"F0.wireOp",EDGE,"E81"),sQuery(id+"F0.wireOp",EDGE,"E82"),sQuery(id+"F0.wireOp",EDGE,"E83"),sQuery(id+"F0.wireOp",EDGE,"E84"),sQuery(id+"F0.wireOp",EDGE,"E85"),sQuery(id+"F0.wireOp",EDGE,"E86"),sQuery(id+"F0.wireOp",EDGE,"E87"),sQuery(id+"F0.wireOp",EDGE,"E88"),sQuery(id+"F0.wireOp",EDGE,"E89"),sQuery(id+"F0.wireOp",EDGE,"E90"),sQuery(id+"F0.wireOp",EDGE,"E91"),sQuery(id+"F0.wireOp",EDGE,"E92"),sQuery(id+"F0.wireOp",EDGE,"E93"),sQuery(id+"F0.wireOp",EDGE,"E94"),sQuery(id+"F0.wireOp",EDGE,"E95"),sQuery(id+"F0.wireOp",EDGE,"E96"),sQuery(id+"F0.wireOp",EDGE,"E97"),sQuery(id+"F0.wireOp",EDGE,"E98"),sQuery(id+"F0.wireOp",EDGE,"E99"),sQuery(id+"F0.wireOp",EDGE,"E100"),sQuery(id+"F0.wireOp",EDGE,"E101"),sQuery(id+"F0.wireOp",EDGE,"E102"),sQuery(id+"F0.wireOp",EDGE,"E103"),sQuery(id+"F0.wireOp",EDGE,"E104"),sQuery(id+"F0.wireOp",EDGE,"E105"),sQuery(id+"F0.wireOp",EDGE,"E106"),sQuery(id+"F0.wireOp",EDGE,"E107"),sQuery(id+"F0.wireOp",EDGE,"E108"),sQuery(id+"F0.wireOp",EDGE,"E109"),sQuery(id+"F0.wireOp",EDGE,"E110"),sQuery(id+"F0.wireOp",EDGE,"E111"),sQuery(id+"F0.wireOp",EDGE,"E112"),sQuery(id+"F0.wireOp",EDGE,"E113"),sQuery(id+"F0.wireOp",EDGE,"E114"),sQuery(id+"F0.wireOp",EDGE,"E115"),sQuery(id+"F0.wireOp",EDGE,"E116"),sQuery(id+"F0.wireOp",EDGE,"E117"),sQuery(id+"F0.wireOp",EDGE,"E118"),sQuery(id+"F0.wireOp",EDGE,"E119"),sQuery(id+"F0.wireOp",EDGE,"E120"),sQuery(id+"F0.wireOp",EDGE,"E121"),sQuery(id+"F0.wireOp",EDGE,"E122"),sQuery(id+"F0.wireOp",EDGE,"E123"),sQuery(id+"F0.wireOp",EDGE,"E124"),sQuery(id+"F0.wireOp",EDGE,"E125"),sQuery(id+"F0.wireOp",EDGE,"E126"),sQuery(id+"F0.wireOp",EDGE,"E127"),sQuery(id+"F0.wireOp",EDGE,"E128"),sQuery(id+"F0.wireOp",EDGE,"E129"),sQuery(id+"F0.wireOp",EDGE,"E130"),sQuery(id+"F0.wireOp",EDGE,"E131"),sQuery(id+"F0.wireOp",EDGE,"E132"),sQuery(id+"F0.wireOp",EDGE,"E133"),sQuery(id+"F0.wireOp",EDGE,"E134"),sQuery(id+"F0.wireOp",EDGE,"E135"),sQuery(id+"F0.wireOp",EDGE,"E136"),sQuery(id+"F0.wireOp",EDGE,"E137"),sQuery(id+"F0.wireOp",EDGE,"E138"),sQuery(id+"F0.wireOp",EDGE,"E139"),sQuery(id+"F0.wireOp",EDGE,"E140"),sQuery(id+"F0.wireOp",EDGE,"E141"),sQuery(id+"F0.wireOp",EDGE,"E142"),sQuery(id+"F0.wireOp",EDGE,"E143"),sQuery(id+"F0.wireOp",EDGE,"E144"),sQuery(id+"F0.wireOp",EDGE,"E145"),sQuery(id+"F0.wireOp",EDGE,"E146"),sQuery(id+"F0.wireOp",EDGE,"E147"),sQuery(id+"F0.wireOp",EDGE,"E148"),sQuery(id+"F0.wireOp",EDGE,"E149"),sQuery(id+"F0.wireOp",EDGE,"E150"),sQuery(id+"F0.wireOp",EDGE,"E151"),sQuery(id+"F0.wireOp",EDGE,"E152"),sQuery(id+"F0.wireOp",EDGE,"E153"),sQuery(id+"F0.wireOp",EDGE,"E154"),sQuery(id+"F0.wireOp",EDGE,"E155"),sQuery(id+"F0.wireOp",EDGE,"E156"),sQuery(id+"F0.wireOp",EDGE,"E157")])],"isStart":false});
            var sketch = newSketch(context, id + "F3", { "sketchPlane" : qUnion([Q0])});
            skLineSegment(sketch, "E158.bottom", {"start": v(-2.02, -17.28) * mm, "end": v(-22.02, -17.28) * mm});
            skLineSegment(sketch, "E158.top", {"start": v(-2.02, -29.28) * mm, "end": v(-22.02, -29.28) * mm});
            skLineSegment(sketch, "E158.left", {"start": v(-2.02, -17.28) * mm, "end": v(-2.02, -29.28) * mm});
            skLineSegment(sketch, "E158.right", {"start": v(-22.02, -17.28) * mm, "end": v(-22.02, -29.28) * mm});
            skLineSegment(sketch, "E159", {"start": v(-22.02, -29.28) * mm, "end": v(-54.27, -29.28) * mm});
            skLineSegment(sketch, "E160", {"start": v(-54.27, -29.28) * mm, "end": v(-60.27, -32.74) * mm});
            skLineSegment(sketch, "E161", {"start": v(-60.27, -32.74) * mm, "end": v(-60.27, -46.98) * mm});
            skLineSegment(sketch, "E162", {"start": v(-60.27, -46.98) * mm, "end": v(91.97, -46.98) * mm});
            skLineSegment(sketch, "E163", {"start": v(91.97, -46.98) * mm, "end": v(91.97, -32.74) * mm});
            skLineSegment(sketch, "E164", {"start": v(91.97, -32.74) * mm, "end": v(85.97, -29.28) * mm});
            skLineSegment(sketch, "E165", {"start": v(85.97, -29.28) * mm, "end": v(-2.02, -29.28) * mm});
            skLineSegment(sketch, "E166", {"start": v(-59.8, 4.49) * mm, "end": v(91.5, 4.49) * mm, "construction": true});
            skLineSegment(sketch, "E167", {"start": v(15.85, 4.49) * mm, "end": v(15.85, -46.98) * mm, "construction": true});
            skText(sketch, "E168", { "text": "PILLAR OF AUTUMN", "fontName": "OpenSans-Bold.ttf"});
            skLineSegment(sketch, "E169", {"start": v(-50.27, -46.98) * mm, "end": v(-30.06, -81.98) * mm});
            skLineSegment(sketch, "E170", {"start": v(-30.06, -81.98) * mm, "end": v(61.76, -81.98) * mm});
            skLineSegment(sketch, "E171", {"start": v(61.76, -81.98) * mm, "end": v(81.97, -46.98) * mm});
            skLineSegment(sketch, "E172.0", {"start": v(55.99, -71.98) * mm, "end": v(70.42, -46.98) * mm});
            skLineSegment(sketch, "E172.1", {"start": v(-24.29, -71.98) * mm, "end": v(55.99, -71.98) * mm});
            skLineSegment(sketch, "E172.2", {"start": v(-38.72, -46.98) * mm, "end": v(-24.29, -71.98) * mm});
            const initialGuessF3  = {"E168": [-0.05027, -0.04298, 1, 0, 0.0097]};
            skSetInitialGuess(sketch, initialGuessF3);
            skSolve(sketch);
        }
        {
            var Q0;
            Q0=makeQuery(id+"F3.imprint","IMPRINT",FACE,{"disambiguationData":[TD([[makeQuery(id+"F3.imprint","IMPRINT",EDGE,{"derivedFrom":sQuery(id+"F3.wireOp",EDGE,"E168.sketch_text.stroke-40")}),1.0]])]});
            var Q1;
            Q1=makeQuery(id+"F3.imprint","IMPRINT",FACE,{"disambiguationData":[TD([[makeQuery(id+"F3.imprint","IMPRINT",EDGE,{"derivedFrom":sQuery(id+"F3.wireOp",EDGE,"E168.sketch_text.stroke-44")}),1.0]])]});
            var Q2;
            Q2=makeQuery(id+"F3.imprint","IMPRINT",FACE,{"disambiguationData":[TD([[makeQuery(id+"F3.imprint","IMPRINT",EDGE,{"derivedFrom":sQuery(id+"F3.wireOp",EDGE,"E168.sketch_text.stroke-71")}),1.0]])]});
            var Q3;
            Q3=makeQuery(id+"F3.imprint","IMPRINT",FACE,{"disambiguationData":[TD([[makeQuery(id+"F3.imprint","IMPRINT",EDGE,{"derivedFrom":sQuery(id+"F3.wireOp",EDGE,"E168.sketch_text.stroke-95")}),1.0]])]});
            var Q4;
            Q4=makeQuery(id+"F3.imprint","IMPRINT",FACE,{"disambiguationData":[TD([[makeQuery(id+"F3.imprint","IMPRINT",EDGE,{"derivedFrom":sQuery(id+"F3.wireOp",EDGE,"E168.sketch_text.stroke-0")}),1.0]])]});
            var Q5;
            Q5=makeQuery(id+"F3.imprint","IMPRINT",FACE,{"disambiguationData":[TD([[makeQuery(id+"F3.imprint","IMPRINT",EDGE,{"derivedFrom":sQuery(id+"F3.wireOp",EDGE,"E158.top")}),1.0]])]});
            var Q6;
            {var subQ1=sQuery(id+"F3.wireOp",EDGE,"E158.top");Q6=makeQuery(id+"F3.imprint","IMPRINT",FACE,{"disambiguationData":[TD([[makeQuery(id+"F3.imprint","IMPRINT",EDGE,{"derivedFrom":subQ1}),-1.0]])]});}
            var Q7;
            {var subQ3=sQuery(id+"F3.wireOp",EDGE,"E169");Q7=makeQuery(id+"F3.imprint","IMPRINT",FACE,{"disambiguationData":[TD([[makeQuery(id+"F3.imprint","IMPRINT",EDGE,{"derivedFrom":subQ3}),1.0]])]});}
            var Q8;
            Q8=makeQuery(id+"F1.opExtrude","CAP_FACE",FACE,{"disambiguationData":[OSD([sQuery(id+"F0.wireOp",EDGE,"E0"),sQuery(id+"F0.wireOp",EDGE,"E1"),sQuery(id+"F0.wireOp",EDGE,"E2"),sQuery(id+"F0.wireOp",EDGE,"E3"),sQuery(id+"F0.wireOp",EDGE,"E4"),sQuery(id+"F0.wireOp",EDGE,"E5"),sQuery(id+"F0.wireOp",EDGE,"E6"),sQuery(id+"F0.wireOp",EDGE,"E7"),sQuery(id+"F0.wireOp",EDGE,"E8"),sQuery(id+"F0.wireOp",EDGE,"E9"),sQuery(id+"F0.wireOp",EDGE,"E10"),sQuery(id+"F0.wireOp",EDGE,"E11"),sQuery(id+"F0.wireOp",EDGE,"E12"),sQuery(id+"F0.wireOp",EDGE,"E13"),sQuery(id+"F0.wireOp",EDGE,"E14"),sQuery(id+"F0.wireOp",EDGE,"E15"),sQuery(id+"F0.wireOp",EDGE,"E16"),sQuery(id+"F0.wireOp",EDGE,"E17"),sQuery(id+"F0.wireOp",EDGE,"E18"),sQuery(id+"F0.wireOp",EDGE,"E19"),sQuery(id+"F0.wireOp",EDGE,"E20"),sQuery(id+"F0.wireOp",EDGE,"E21"),sQuery(id+"F0.wireOp",EDGE,"E22"),sQuery(id+"F0.wireOp",EDGE,"E23"),sQuery(id+"F0.wireOp",EDGE,"E24"),sQuery(id+"F0.wireOp",EDGE,"E25"),sQuery(id+"F0.wireOp",EDGE,"E26"),sQuery(id+"F0.wireOp",EDGE,"E27"),sQuery(id+"F0.wireOp",EDGE,"E28"),sQuery(id+"F0.wireOp",EDGE,"E29"),sQuery(id+"F0.wireOp",EDGE,"E30"),sQuery(id+"F0.wireOp",EDGE,"E31"),sQuery(id+"F0.wireOp",EDGE,"E32"),sQuery(id+"F0.wireOp",EDGE,"E33"),sQuery(id+"F0.wireOp",EDGE,"E34"),sQuery(id+"F0.wireOp",EDGE,"E35"),sQuery(id+"F0.wireOp",EDGE,"E36"),sQuery(id+"F0.wireOp",EDGE,"E37"),sQuery(id+"F0.wireOp",EDGE,"E38"),sQuery(id+"F0.wireOp",EDGE,"E39"),sQuery(id+"F0.wireOp",EDGE,"E40"),sQuery(id+"F0.wireOp",EDGE,"E41"),sQuery(id+"F0.wireOp",EDGE,"E42"),sQuery(id+"F0.wireOp",EDGE,"E43"),sQuery(id+"F0.wireOp",EDGE,"E44"),sQuery(id+"F0.wireOp",EDGE,"E45"),sQuery(id+"F0.wireOp",EDGE,"E46"),sQuery(id+"F0.wireOp",EDGE,"E47"),sQuery(id+"F0.wireOp",EDGE,"E48"),sQuery(id+"F0.wireOp",EDGE,"E49"),sQuery(id+"F0.wireOp",EDGE,"E50"),sQuery(id+"F0.wireOp",EDGE,"E51"),sQuery(id+"F0.wireOp",EDGE,"E52"),sQuery(id+"F0.wireOp",EDGE,"E53"),sQuery(id+"F0.wireOp",EDGE,"E54"),sQuery(id+"F0.wireOp",EDGE,"E55"),sQuery(id+"F0.wireOp",EDGE,"E56"),sQuery(id+"F0.wireOp",EDGE,"E57"),sQuery(id+"F0.wireOp",EDGE,"E58"),sQuery(id+"F0.wireOp",EDGE,"E59"),sQuery(id+"F0.wireOp",EDGE,"E60"),sQuery(id+"F0.wireOp",EDGE,"E61"),sQuery(id+"F0.wireOp",EDGE,"E62"),sQuery(id+"F0.wireOp",EDGE,"E63"),sQuery(id+"F0.wireOp",EDGE,"E64"),sQuery(id+"F0.wireOp",EDGE,"E65"),sQuery(id+"F0.wireOp",EDGE,"E66"),sQuery(id+"F0.wireOp",EDGE,"E67"),sQuery(id+"F0.wireOp",EDGE,"E68"),sQuery(id+"F0.wireOp",EDGE,"E69"),sQuery(id+"F0.wireOp",EDGE,"E70"),sQuery(id+"F0.wireOp",EDGE,"E71"),sQuery(id+"F0.wireOp",EDGE,"E72"),sQuery(id+"F0.wireOp",EDGE,"E73"),sQuery(id+"F0.wireOp",EDGE,"E74"),sQuery(id+"F0.wireOp",EDGE,"E75"),sQuery(id+"F0.wireOp",EDGE,"E76"),sQuery(id+"F0.wireOp",EDGE,"E77"),sQuery(id+"F0.wireOp",EDGE,"E78"),sQuery(id+"F0.wireOp",EDGE,"E79"),sQuery(id+"F0.wireOp",EDGE,"E80"),sQuery(id+"F0.wireOp",EDGE,"E81"),sQuery(id+"F0.wireOp",EDGE,"E82"),sQuery(id+"F0.wireOp",EDGE,"E83"),sQuery(id+"F0.wireOp",EDGE,"E84"),sQuery(id+"F0.wireOp",EDGE,"E85"),sQuery(id+"F0.wireOp",EDGE,"E86"),sQuery(id+"F0.wireOp",EDGE,"E87"),sQuery(id+"F0.wireOp",EDGE,"E88"),sQuery(id+"F0.wireOp",EDGE,"E89"),sQuery(id+"F0.wireOp",EDGE,"E90"),sQuery(id+"F0.wireOp",EDGE,"E91"),sQuery(id+"F0.wireOp",EDGE,"E92"),sQuery(id+"F0.wireOp",EDGE,"E93"),sQuery(id+"F0.wireOp",EDGE,"E94"),sQuery(id+"F0.wireOp",EDGE,"E95"),sQuery(id+"F0.wireOp",EDGE,"E96"),sQuery(id+"F0.wireOp",EDGE,"E97"),sQuery(id+"F0.wireOp",EDGE,"E98"),sQuery(id+"F0.wireOp",EDGE,"E99"),sQuery(id+"F0.wireOp",EDGE,"E100"),sQuery(id+"F0.wireOp",EDGE,"E101"),sQuery(id+"F0.wireOp",EDGE,"E102"),sQuery(id+"F0.wireOp",EDGE,"E103"),sQuery(id+"F0.wireOp",EDGE,"E104"),sQuery(id+"F0.wireOp",EDGE,"E105"),sQuery(id+"F0.wireOp",EDGE,"E106"),sQuery(id+"F0.wireOp",EDGE,"E107"),sQuery(id+"F0.wireOp",EDGE,"E108"),sQuery(id+"F0.wireOp",EDGE,"E109"),sQuery(id+"F0.wireOp",EDGE,"E110"),sQuery(id+"F0.wireOp",EDGE,"E111"),sQuery(id+"F0.wireOp",EDGE,"E112"),sQuery(id+"F0.wireOp",EDGE,"E113"),sQuery(id+"F0.wireOp",EDGE,"E114"),sQuery(id+"F0.wireOp",EDGE,"E115"),sQuery(id+"F0.wireOp",EDGE,"E116"),sQuery(id+"F0.wireOp",EDGE,"E117"),sQuery(id+"F0.wireOp",EDGE,"E118"),sQuery(id+"F0.wireOp",EDGE,"E119"),sQuery(id+"F0.wireOp",EDGE,"E120"),sQuery(id+"F0.wireOp",EDGE,"E121"),sQuery(id+"F0.wireOp",EDGE,"E122"),sQuery(id+"F0.wireOp",EDGE,"E123"),sQuery(id+"F0.wireOp",EDGE,"E124"),sQuery(id+"F0.wireOp",EDGE,"E125"),sQuery(id+"F0.wireOp",EDGE,"E126"),sQuery(id+"F0.wireOp",EDGE,"E127"),sQuery(id+"F0.wireOp",EDGE,"E128"),sQuery(id+"F0.wireOp",EDGE,"E129"),sQuery(id+"F0.wireOp",EDGE,"E130"),sQuery(id+"F0.wireOp",EDGE,"E131"),sQuery(id+"F0.wireOp",EDGE,"E132"),sQuery(id+"F0.wireOp",EDGE,"E133"),sQuery(id+"F0.wireOp",EDGE,"E134"),sQuery(id+"F0.wireOp",EDGE,"E135"),sQuery(id+"F0.wireOp",EDGE,"E136"),sQuery(id+"F0.wireOp",EDGE,"E137"),sQuery(id+"F0.wireOp",EDGE,"E138"),sQuery(id+"F0.wireOp",EDGE,"E139"),sQuery(id+"F0.wireOp",EDGE,"E140"),sQuery(id+"F0.wireOp",EDGE,"E141"),sQuery(id+"F0.wireOp",EDGE,"E142"),sQuery(id+"F0.wireOp",EDGE,"E143"),sQuery(id+"F0.wireOp",EDGE,"E144"),sQuery(id+"F0.wireOp",EDGE,"E145"),sQuery(id+"F0.wireOp",EDGE,"E146"),sQuery(id+"F0.wireOp",EDGE,"E147"),sQuery(id+"F0.wireOp",EDGE,"E148"),sQuery(id+"F0.wireOp",EDGE,"E149"),sQuery(id+"F0.wireOp",EDGE,"E150"),sQuery(id+"F0.wireOp",EDGE,"E151"),sQuery(id+"F0.wireOp",EDGE,"E152"),sQuery(id+"F0.wireOp",EDGE,"E153"),sQuery(id+"F0.wireOp",EDGE,"E154"),sQuery(id+"F0.wireOp",EDGE,"E155"),sQuery(id+"F0.wireOp",EDGE,"E156"),sQuery(id+"F0.wireOp",EDGE,"E157")])],"isStart":true});
            extrude(context, id + "F4", {"entities" : qUnion([Q0, Q1, Q2, Q3, Q4, Q5, Q6, Q7]), "operationType" : NewBodyOperationType.ADD, "endBound" : BoundingType.UP_TO_SURFACE, "oppositeDirection" : true, "depth" : 25 * mm, "endBoundEntityFace" : qUnion([Q8]), "offsetDistance" : 25 * mm});
        }
        {
            var Q0;
            {var subQ0=sQuery(id+"F0.wireOp",EDGE,"E124");var subQ1=sQuery(id+"F0.wireOp",EDGE,"E123");Q0=makeQuery(id+"F4.boolean.opBoolean","MERGE",FACE,{"derivedFrom":[makeQuery(id+"F1.opExtrude","CAP_FACE",FACE,{"disambiguationData":[OSD([sQuery(id+"F0.wireOp",EDGE,"E0"),sQuery(id+"F0.wireOp",EDGE,"E1"),sQuery(id+"F0.wireOp",EDGE,"E2"),sQuery(id+"F0.wireOp",EDGE,"E3"),sQuery(id+"F0.wireOp",EDGE,"E4"),sQuery(id+"F0.wireOp",EDGE,"E5"),sQuery(id+"F0.wireOp",EDGE,"E6"),sQuery(id+"F0.wireOp",EDGE,"E7"),sQuery(id+"F0.wireOp",EDGE,"E8"),sQuery(id+"F0.wireOp",EDGE,"E9"),sQuery(id+"F0.wireOp",EDGE,"E10"),sQuery(id+"F0.wireOp",EDGE,"E11"),sQuery(id+"F0.wireOp",EDGE,"E12"),sQuery(id+"F0.wireOp",EDGE,"E13"),sQuery(id+"F0.wireOp",EDGE,"E14"),sQuery(id+"F0.wireOp",EDGE,"E15"),sQuery(id+"F0.wireOp",EDGE,"E16"),sQuery(id+"F0.wireOp",EDGE,"E17"),sQuery(id+"F0.wireOp",EDGE,"E18"),sQuery(id+"F0.wireOp",EDGE,"E19"),sQuery(id+"F0.wireOp",EDGE,"E20"),sQuery(id+"F0.wireOp",EDGE,"E21"),sQuery(id+"F0.wireOp",EDGE,"E22"),sQuery(id+"F0.wireOp",EDGE,"E23"),sQuery(id+"F0.wireOp",EDGE,"E24"),sQuery(id+"F0.wireOp",EDGE,"E25"),sQuery(id+"F0.wireOp",EDGE,"E26"),sQuery(id+"F0.wireOp",EDGE,"E27"),sQuery(id+"F0.wireOp",EDGE,"E28"),sQuery(id+"F0.wireOp",EDGE,"E29"),sQuery(id+"F0.wireOp",EDGE,"E30"),sQuery(id+"F0.wireOp",EDGE,"E31"),sQuery(id+"F0.wireOp",EDGE,"E32"),sQuery(id+"F0.wireOp",EDGE,"E33"),sQuery(id+"F0.wireOp",EDGE,"E34"),sQuery(id+"F0.wireOp",EDGE,"E35"),sQuery(id+"F0.wireOp",EDGE,"E36"),sQuery(id+"F0.wireOp",EDGE,"E37"),sQuery(id+"F0.wireOp",EDGE,"E38"),sQuery(id+"F0.wireOp",EDGE,"E39"),sQuery(id+"F0.wireOp",EDGE,"E40"),sQuery(id+"F0.wireOp",EDGE,"E41"),sQuery(id+"F0.wireOp",EDGE,"E42"),sQuery(id+"F0.wireOp",EDGE,"E43"),sQuery(id+"F0.wireOp",EDGE,"E44"),sQuery(id+"F0.wireOp",EDGE,"E45"),sQuery(id+"F0.wireOp",EDGE,"E46"),sQuery(id+"F0.wireOp",EDGE,"E47"),sQuery(id+"F0.wireOp",EDGE,"E48"),sQuery(id+"F0.wireOp",EDGE,"E49"),sQuery(id+"F0.wireOp",EDGE,"E50"),sQuery(id+"F0.wireOp",EDGE,"E51"),sQuery(id+"F0.wireOp",EDGE,"E52"),sQuery(id+"F0.wireOp",EDGE,"E53"),sQuery(id+"F0.wireOp",EDGE,"E54"),sQuery(id+"F0.wireOp",EDGE,"E55"),sQuery(id+"F0.wireOp",EDGE,"E56"),sQuery(id+"F0.wireOp",EDGE,"E57"),sQuery(id+"F0.wireOp",EDGE,"E58"),sQuery(id+"F0.wireOp",EDGE,"E59"),sQuery(id+"F0.wireOp",EDGE,"E60"),sQuery(id+"F0.wireOp",EDGE,"E61"),sQuery(id+"F0.wireOp",EDGE,"E62"),sQuery(id+"F0.wireOp",EDGE,"E63"),sQuery(id+"F0.wireOp",EDGE,"E64"),sQuery(id+"F0.wireOp",EDGE,"E65"),sQuery(id+"F0.wireOp",EDGE,"E66"),sQuery(id+"F0.wireOp",EDGE,"E67"),sQuery(id+"F0.wireOp",EDGE,"E68"),sQuery(id+"F0.wireOp",EDGE,"E69"),sQuery(id+"F0.wireOp",EDGE,"E70"),sQuery(id+"F0.wireOp",EDGE,"E71"),sQuery(id+"F0.wireOp",EDGE,"E72"),sQuery(id+"F0.wireOp",EDGE,"E73"),sQuery(id+"F0.wireOp",EDGE,"E74"),sQuery(id+"F0.wireOp",EDGE,"E75"),sQuery(id+"F0.wireOp",EDGE,"E76"),sQuery(id+"F0.wireOp",EDGE,"E77"),sQuery(id+"F0.wireOp",EDGE,"E78"),sQuery(id+"F0.wireOp",EDGE,"E79"),sQuery(id+"F0.wireOp",EDGE,"E80"),sQuery(id+"F0.wireOp",EDGE,"E81"),sQuery(id+"F0.wireOp",EDGE,"E82"),sQuery(id+"F0.wireOp",EDGE,"E83"),sQuery(id+"F0.wireOp",EDGE,"E84"),sQuery(id+"F0.wireOp",EDGE,"E85"),sQuery(id+"F0.wireOp",EDGE,"E86"),sQuery(id+"F0.wireOp",EDGE,"E87"),sQuery(id+"F0.wireOp",EDGE,"E88"),sQuery(id+"F0.wireOp",EDGE,"E89"),sQuery(id+"F0.wireOp",EDGE,"E90"),sQuery(id+"F0.wireOp",EDGE,"E91"),sQuery(id+"F0.wireOp",EDGE,"E92"),sQuery(id+"F0.wireOp",EDGE,"E93"),sQuery(id+"F0.wireOp",EDGE,"E94"),sQuery(id+"F0.wireOp",EDGE,"E95"),sQuery(id+"F0.wireOp",EDGE,"E96"),sQuery(id+"F0.wireOp",EDGE,"E97"),sQuery(id+"F0.wireOp",EDGE,"E98"),sQuery(id+"F0.wireOp",EDGE,"E99"),sQuery(id+"F0.wireOp",EDGE,"E100"),sQuery(id+"F0.wireOp",EDGE,"E101"),sQuery(id+"F0.wireOp",EDGE,"E102"),sQuery(id+"F0.wireOp",EDGE,"E103"),sQuery(id+"F0.wireOp",EDGE,"E104"),sQuery(id+"F0.wireOp",EDGE,"E105"),sQuery(id+"F0.wireOp",EDGE,"E106"),sQuery(id+"F0.wireOp",EDGE,"E107"),sQuery(id+"F0.wireOp",EDGE,"E108"),sQuery(id+"F0.wireOp",EDGE,"E109"),sQuery(id+"F0.wireOp",EDGE,"E110"),sQuery(id+"F0.wireOp",EDGE,"E111"),sQuery(id+"F0.wireOp",EDGE,"E112"),sQuery(id+"F0.wireOp",EDGE,"E113"),sQuery(id+"F0.wireOp",EDGE,"E114"),sQuery(id+"F0.wireOp",EDGE,"E115"),sQuery(id+"F0.wireOp",EDGE,"E116"),sQuery(id+"F0.wireOp",EDGE,"E117"),sQuery(id+"F0.wireOp",EDGE,"E118"),sQuery(id+"F0.wireOp",EDGE,"E119"),sQuery(id+"F0.wireOp",EDGE,"E120"),sQuery(id+"F0.wireOp",EDGE,"E121"),sQuery(id+"F0.wireOp",EDGE,"E122"),subQ1,subQ0,sQuery(id+"F0.wireOp",EDGE,"E125"),sQuery(id+"F0.wireOp",EDGE,"E126"),sQuery(id+"F0.wireOp",EDGE,"E127"),sQuery(id+"F0.wireOp",EDGE,"E128"),sQuery(id+"F0.wireOp",EDGE,"E129"),sQuery(id+"F0.wireOp",EDGE,"E130"),sQuery(id+"F0.wireOp",EDGE,"E131"),sQuery(id+"F0.wireOp",EDGE,"E132"),sQuery(id+"F0.wireOp",EDGE,"E133"),sQuery(id+"F0.wireOp",EDGE,"E134"),sQuery(id+"F0.wireOp",EDGE,"E135"),sQuery(id+"F0.wireOp",EDGE,"E136"),sQuery(id+"F0.wireOp",EDGE,"E137"),sQuery(id+"F0.wireOp",EDGE,"E138"),sQuery(id+"F0.wireOp",EDGE,"E139"),sQuery(id+"F0.wireOp",EDGE,"E140"),sQuery(id+"F0.wireOp",EDGE,"E141"),sQuery(id+"F0.wireOp",EDGE,"E142"),sQuery(id+"F0.wireOp",EDGE,"E143"),sQuery(id+"F0.wireOp",EDGE,"E144"),sQuery(id+"F0.wireOp",EDGE,"E145"),sQuery(id+"F0.wireOp",EDGE,"E146"),sQuery(id+"F0.wireOp",EDGE,"E147"),sQuery(id+"F0.wireOp",EDGE,"E148"),sQuery(id+"F0.wireOp",EDGE,"E149"),sQuery(id+"F0.wireOp",EDGE,"E150"),sQuery(id+"F0.wireOp",EDGE,"E151"),sQuery(id+"F0.wireOp",EDGE,"E152"),sQuery(id+"F0.wireOp",EDGE,"E153"),sQuery(id+"F0.wireOp",EDGE,"E154"),sQuery(id+"F0.wireOp",EDGE,"E155"),sQuery(id+"F0.wireOp",EDGE,"E156"),sQuery(id+"F0.wireOp",EDGE,"E157")])],"isStart":false}),makeQuery(id+"F4.opExtrude","CAP_FACE",FACE,{"disambiguationData":[OSD([subQ1,subQ0,sQuery(id+"F3.wireOp",EDGE,"E158.bottom"),sQuery(id+"F3.wireOp",EDGE,"E158.left"),sQuery(id+"F3.wireOp",EDGE,"E158.right"),sQuery(id+"F3.wireOp",EDGE,"E159"),sQuery(id+"F3.wireOp",EDGE,"E160"),sQuery(id+"F3.wireOp",EDGE,"E161"),sQuery(id+"F3.wireOp",EDGE,"E162"),sQuery(id+"F3.wireOp",EDGE,"E163"),sQuery(id+"F3.wireOp",EDGE,"E164"),sQuery(id+"F3.wireOp",EDGE,"E165"),sQuery(id+"F3.wireOp",EDGE,"E168.sketch_text.stroke-7"),sQuery(id+"F3.wireOp",EDGE,"E168.sketch_text.stroke-8"),sQuery(id+"F3.wireOp",EDGE,"E168.sketch_text.stroke-9"),sQuery(id+"F3.wireOp",EDGE,"E168.sketch_text.stroke-10"),sQuery(id+"F3.wireOp",EDGE,"E168.sketch_text.stroke-11"),sQuery(id+"F3.wireOp",EDGE,"E168.sketch_text.stroke-12"),sQuery(id+"F3.wireOp",EDGE,"E168.sketch_text.stroke-13"),sQuery(id+"F3.wireOp",EDGE,"E168.sketch_text.stroke-14"),sQuery(id+"F3.wireOp",EDGE,"E168.sketch_text.stroke-15"),sQuery(id+"F3.wireOp",EDGE,"E168.sketch_text.stroke-16"),sQuery(id+"F3.wireOp",EDGE,"E168.sketch_text.stroke-17"),sQuery(id+"F3.wireOp",EDGE,"E168.sketch_text.stroke-18"),sQuery(id+"F3.wireOp",EDGE,"E168.sketch_text.stroke-19"),sQuery(id+"F3.wireOp",EDGE,"E168.sketch_text.stroke-20"),sQuery(id+"F3.wireOp",EDGE,"E168.sketch_text.stroke-21"),sQuery(id+"F3.wireOp",EDGE,"E168.sketch_text.stroke-22"),sQuery(id+"F3.wireOp",EDGE,"E168.sketch_text.stroke-23"),sQuery(id+"F3.wireOp",EDGE,"E168.sketch_text.stroke-24"),sQuery(id+"F3.wireOp",EDGE,"E168.sketch_text.stroke-25"),sQuery(id+"F3.wireOp",EDGE,"E168.sketch_text.stroke-26"),sQuery(id+"F3.wireOp",EDGE,"E168.sketch_text.stroke-27"),sQuery(id+"F3.wireOp",EDGE,"E168.sketch_text.stroke-28"),sQuery(id+"F3.wireOp",EDGE,"E168.sketch_text.stroke-29"),sQuery(id+"F3.wireOp",EDGE,"E168.sketch_text.stroke-30"),sQuery(id+"F3.wireOp",EDGE,"E168.sketch_text.stroke-31"),sQuery(id+"F3.wireOp",EDGE,"E168.sketch_text.stroke-32"),sQuery(id+"F3.wireOp",EDGE,"E168.sketch_text.stroke-33"),sQuery(id+"F3.wireOp",EDGE,"E168.sketch_text.stroke-34"),sQuery(id+"F3.wireOp",EDGE,"E168.sketch_text.stroke-35"),sQuery(id+"F3.wireOp",EDGE,"E168.sketch_text.stroke-36"),sQuery(id+"F3.wireOp",EDGE,"E168.sketch_text.stroke-37"),sQuery(id+"F3.wireOp",EDGE,"E168.sketch_text.stroke-38"),sQuery(id+"F3.wireOp",EDGE,"E168.sketch_text.stroke-39"),sQuery(id+"F3.wireOp",EDGE,"E168.sketch_text.stroke-51"),sQuery(id+"F3.wireOp",EDGE,"E168.sketch_text.stroke-52"),sQuery(id+"F3.wireOp",EDGE,"E168.sketch_text.stroke-53"),sQuery(id+"F3.wireOp",EDGE,"E168.sketch_text.stroke-54"),sQuery(id+"F3.wireOp",EDGE,"E168.sketch_text.stroke-55"),sQuery(id+"F3.wireOp",EDGE,"E168.sketch_text.stroke-56"),sQuery(id+"F3.wireOp",EDGE,"E168.sketch_text.stroke-57"),sQuery(id+"F3.wireOp",EDGE,"E168.sketch_text.stroke-58"),sQuery(id+"F3.wireOp",EDGE,"E168.sketch_text.stroke-59"),sQuery(id+"F3.wireOp",EDGE,"E168.sketch_text.stroke-60"),sQuery(id+"F3.wireOp",EDGE,"E168.sketch_text.stroke-61"),sQuery(id+"F3.wireOp",EDGE,"E168.sketch_text.stroke-62"),sQuery(id+"F3.wireOp",EDGE,"E168.sketch_text.stroke-63"),sQuery(id+"F3.wireOp",EDGE,"E168.sketch_text.stroke-64"),sQuery(id+"F3.wireOp",EDGE,"E168.sketch_text.stroke-65"),sQuery(id+"F3.wireOp",EDGE,"E168.sketch_text.stroke-66"),sQuery(id+"F3.wireOp",EDGE,"E168.sketch_text.stroke-67"),sQuery(id+"F3.wireOp",EDGE,"E168.sketch_text.stroke-68"),sQuery(id+"F3.wireOp",EDGE,"E168.sketch_text.stroke-69"),sQuery(id+"F3.wireOp",EDGE,"E168.sketch_text.stroke-70"),sQuery(id+"F3.wireOp",EDGE,"E168.sketch_text.stroke-77"),sQuery(id+"F3.wireOp",EDGE,"E168.sketch_text.stroke-78"),sQuery(id+"F3.wireOp",EDGE,"E168.sketch_text.stroke-79"),sQuery(id+"F3.wireOp",EDGE,"E168.sketch_text.stroke-80"),sQuery(id+"F3.wireOp",EDGE,"E168.sketch_text.stroke-81"),sQuery(id+"F3.wireOp",EDGE,"E168.sketch_text.stroke-82"),sQuery(id+"F3.wireOp",EDGE,"E168.sketch_text.stroke-83"),sQuery(id+"F3.wireOp",EDGE,"E168.sketch_text.stroke-84"),sQuery(id+"F3.wireOp",EDGE,"E168.sketch_text.stroke-85"),sQuery(id+"F3.wireOp",EDGE,"E168.sketch_text.stroke-86"),sQuery(id+"F3.wireOp",EDGE,"E168.sketch_text.stroke-87"),sQuery(id+"F3.wireOp",EDGE,"E168.sketch_text.stroke-88"),sQuery(id+"F3.wireOp",EDGE,"E168.sketch_text.stroke-89"),sQuery(id+"F3.wireOp",EDGE,"E168.sketch_text.stroke-90"),sQuery(id+"F3.wireOp",EDGE,"E168.sketch_text.stroke-91"),sQuery(id+"F3.wireOp",EDGE,"E168.sketch_text.stroke-92"),sQuery(id+"F3.wireOp",EDGE,"E168.sketch_text.stroke-93"),sQuery(id+"F3.wireOp",EDGE,"E168.sketch_text.stroke-94"),sQuery(id+"F3.wireOp",EDGE,"E168.sketch_text.stroke-99"),sQuery(id+"F3.wireOp",EDGE,"E168.sketch_text.stroke-100"),sQuery(id+"F3.wireOp",EDGE,"E168.sketch_text.stroke-101"),sQuery(id+"F3.wireOp",EDGE,"E168.sketch_text.stroke-102"),sQuery(id+"F3.wireOp",EDGE,"E168.sketch_text.stroke-103"),sQuery(id+"F3.wireOp",EDGE,"E168.sketch_text.stroke-104"),sQuery(id+"F3.wireOp",EDGE,"E168.sketch_text.stroke-105"),sQuery(id+"F3.wireOp",EDGE,"E168.sketch_text.stroke-106"),sQuery(id+"F3.wireOp",EDGE,"E168.sketch_text.stroke-107"),sQuery(id+"F3.wireOp",EDGE,"E168.sketch_text.stroke-108"),sQuery(id+"F3.wireOp",EDGE,"E168.sketch_text.stroke-109"),sQuery(id+"F3.wireOp",EDGE,"E168.sketch_text.stroke-110"),sQuery(id+"F3.wireOp",EDGE,"E168.sketch_text.stroke-111"),sQuery(id+"F3.wireOp",EDGE,"E168.sketch_text.stroke-112"),sQuery(id+"F3.wireOp",EDGE,"E168.sketch_text.stroke-113"),sQuery(id+"F3.wireOp",EDGE,"E168.sketch_text.stroke-114"),sQuery(id+"F3.wireOp",EDGE,"E168.sketch_text.stroke-115"),sQuery(id+"F3.wireOp",EDGE,"E168.sketch_text.stroke-116"),sQuery(id+"F3.wireOp",EDGE,"E168.sketch_text.stroke-117"),sQuery(id+"F3.wireOp",EDGE,"E168.sketch_text.stroke-118"),sQuery(id+"F3.wireOp",EDGE,"E168.sketch_text.stroke-119"),sQuery(id+"F3.wireOp",EDGE,"E168.sketch_text.stroke-120"),sQuery(id+"F3.wireOp",EDGE,"E168.sketch_text.stroke-121"),sQuery(id+"F3.wireOp",EDGE,"E168.sketch_text.stroke-122"),sQuery(id+"F3.wireOp",EDGE,"E168.sketch_text.stroke-123"),sQuery(id+"F3.wireOp",EDGE,"E168.sketch_text.stroke-124"),sQuery(id+"F3.wireOp",EDGE,"E168.sketch_text.stroke-125"),sQuery(id+"F3.wireOp",EDGE,"E168.sketch_text.stroke-126"),sQuery(id+"F3.wireOp",EDGE,"E168.sketch_text.stroke-127"),sQuery(id+"F3.wireOp",EDGE,"E168.sketch_text.stroke-128"),sQuery(id+"F3.wireOp",EDGE,"E168.sketch_text.stroke-129"),sQuery(id+"F3.wireOp",EDGE,"E168.sketch_text.stroke-130"),sQuery(id+"F3.wireOp",EDGE,"E168.sketch_text.stroke-131"),sQuery(id+"F3.wireOp",EDGE,"E168.sketch_text.stroke-132"),sQuery(id+"F3.wireOp",EDGE,"E168.sketch_text.stroke-133"),sQuery(id+"F3.wireOp",EDGE,"E168.sketch_text.stroke-134"),sQuery(id+"F3.wireOp",EDGE,"E168.sketch_text.stroke-135"),sQuery(id+"F3.wireOp",EDGE,"E168.sketch_text.stroke-136"),sQuery(id+"F3.wireOp",EDGE,"E168.sketch_text.stroke-137"),sQuery(id+"F3.wireOp",EDGE,"E168.sketch_text.stroke-138"),sQuery(id+"F3.wireOp",EDGE,"E168.sketch_text.stroke-139"),sQuery(id+"F3.wireOp",EDGE,"E168.sketch_text.stroke-140"),sQuery(id+"F3.wireOp",EDGE,"E168.sketch_text.stroke-141"),sQuery(id+"F3.wireOp",EDGE,"E168.sketch_text.stroke-142"),sQuery(id+"F3.wireOp",EDGE,"E168.sketch_text.stroke-143"),sQuery(id+"F3.wireOp",EDGE,"E168.sketch_text.stroke-144"),sQuery(id+"F3.wireOp",EDGE,"E168.sketch_text.stroke-145"),sQuery(id+"F3.wireOp",EDGE,"E168.sketch_text.stroke-146"),sQuery(id+"F3.wireOp",EDGE,"E168.sketch_text.stroke-147"),sQuery(id+"F3.wireOp",EDGE,"E168.sketch_text.stroke-148"),sQuery(id+"F3.wireOp",EDGE,"E168.sketch_text.stroke-149"),sQuery(id+"F3.wireOp",EDGE,"E168.sketch_text.stroke-150"),sQuery(id+"F3.wireOp",EDGE,"E168.sketch_text.stroke-151"),sQuery(id+"F3.wireOp",EDGE,"E168.sketch_text.stroke-152"),sQuery(id+"F3.wireOp",EDGE,"E168.sketch_text.stroke-153"),sQuery(id+"F3.wireOp",EDGE,"E168.sketch_text.stroke-154"),sQuery(id+"F3.wireOp",EDGE,"E168.sketch_text.stroke-155"),sQuery(id+"F3.wireOp",EDGE,"E168.sketch_text.stroke-156"),sQuery(id+"F3.wireOp",EDGE,"E168.sketch_text.stroke-157"),sQuery(id+"F3.wireOp",EDGE,"E168.sketch_text.stroke-158"),sQuery(id+"F3.wireOp",EDGE,"E168.sketch_text.stroke-159"),sQuery(id+"F3.wireOp",EDGE,"E168.sketch_text.stroke-160"),sQuery(id+"F3.wireOp",EDGE,"E168.sketch_text.stroke-161"),sQuery(id+"F3.wireOp",EDGE,"E168.sketch_text.stroke-162"),sQuery(id+"F3.wireOp",EDGE,"E168.sketch_text.stroke-163"),sQuery(id+"F3.wireOp",EDGE,"E168.sketch_text.stroke-164"),sQuery(id+"F3.wireOp",EDGE,"E168.sketch_text.stroke-165"),sQuery(id+"F3.wireOp",EDGE,"E168.sketch_text.stroke-166"),sQuery(id+"F3.wireOp",EDGE,"E168.sketch_text.stroke-167"),sQuery(id+"F3.wireOp",EDGE,"E168.sketch_text.stroke-168"),sQuery(id+"F3.wireOp",EDGE,"E168.sketch_text.stroke-169"),sQuery(id+"F3.wireOp",EDGE,"E169"),sQuery(id+"F3.wireOp",EDGE,"E170"),sQuery(id+"F3.wireOp",EDGE,"E171"),sQuery(id+"F3.wireOp",EDGE,"E172.0"),sQuery(id+"F3.wireOp",EDGE,"E172.1"),sQuery(id+"F3.wireOp",EDGE,"E172.2")])],"isStart":true})]});}
            var sketch = newSketch(context, id + "F5", { "sketchPlane" : qUnion([Q0])});
            skLineSegment(sketch, "E173.bottom", {"start": v(-47.02, -39.56) * mm, "end": v(-45.72, -39.56) * mm});
            skLineSegment(sketch, "E173.top", {"start": v(-47.02, -33.36) * mm, "end": v(-45.72, -33.36) * mm});
            skLineSegment(sketch, "E173.left", {"start": v(-47.02, -39.56) * mm, "end": v(-47.02, -33.36) * mm});
            skLineSegment(sketch, "E173.right", {"start": v(-45.72, -39.56) * mm, "end": v(-45.72, -33.36) * mm});
            skPoint(sketch, "E174.firstSnap0", {"position": v(-17.48, -40.69) * mm});
            skLineSegment(sketch, "E174.bottom", {"start": v(-18.13, -40.69) * mm, "end": v(-16.83, -40.69) * mm});
            skLineSegment(sketch, "E174.top", {"start": v(-18.13, -33.32) * mm, "end": v(-16.83, -33.32) * mm});
            skLineSegment(sketch, "E174.left", {"start": v(-16.83, -40.69) * mm, "end": v(-16.83, -33.32) * mm});
            skLineSegment(sketch, "E174.right", {"start": v(-18.13, -40.69) * mm, "end": v(-18.13, -33.32) * mm});
            skLineSegment(sketch, "E175.bottom", {"start": v(-9.58, -39.63) * mm, "end": v(-8.28, -39.63) * mm});
            skLineSegment(sketch, "E175.top", {"start": v(-9.58, -33.36) * mm, "end": v(-8.28, -33.36) * mm});
            skLineSegment(sketch, "E175.left", {"start": v(-9.58, -39.63) * mm, "end": v(-9.58, -33.36) * mm});
            skLineSegment(sketch, "E175.right", {"start": v(-8.28, -39.63) * mm, "end": v(-8.28, -33.36) * mm});
            skLineSegment(sketch, "E176.bottom", {"start": v(4.3, -33.2) * mm, "end": v(5.6, -33.2) * mm});
            skLineSegment(sketch, "E176.top", {"start": v(4.3, -43.1) * mm, "end": v(5.6, -43.1) * mm});
            skLineSegment(sketch, "E176.left", {"start": v(4.3, -33.2) * mm, "end": v(4.3, -43.1) * mm});
            skLineSegment(sketch, "E176.right", {"start": v(5.6, -33.2) * mm, "end": v(5.6, -43.1) * mm});
            skLineSegment(sketch, "E177.bottom", {"start": v(25.18, -33.32) * mm, "end": v(26.48, -33.32) * mm});
            skLineSegment(sketch, "E177.top", {"start": v(25.18, -40.69) * mm, "end": v(26.48, -40.69) * mm});
            skLineSegment(sketch, "E177.left", {"start": v(25.18, -33.32) * mm, "end": v(25.18, -40.69) * mm});
            skLineSegment(sketch, "E178", {"start": v(26.48, -33.32) * mm, "end": v(26.48, -40.69) * mm});
            skSolve(sketch);
        }
        {
            var Q0;
            Q0 = qSketchRegion(id + "F5", true);
            var Q1;
            {var subQ0=sQuery(id+"F0.wireOp",EDGE,"E157");var subQ1=sQuery(id+"F0.wireOp",EDGE,"E156");var subQ2=sQuery(id+"F0.wireOp",EDGE,"E155");var subQ3=sQuery(id+"F0.wireOp",EDGE,"E154");var subQ4=sQuery(id+"F0.wireOp",EDGE,"E153");var subQ5=sQuery(id+"F0.wireOp",EDGE,"E152");var subQ6=sQuery(id+"F0.wireOp",EDGE,"E151");var subQ7=sQuery(id+"F0.wireOp",EDGE,"E150");var subQ8=sQuery(id+"F0.wireOp",EDGE,"E149");var subQ9=sQuery(id+"F0.wireOp",EDGE,"E148");var subQ10=sQuery(id+"F0.wireOp",EDGE,"E147");var subQ11=sQuery(id+"F0.wireOp",EDGE,"E146");var subQ12=sQuery(id+"F0.wireOp",EDGE,"E145");var subQ13=sQuery(id+"F0.wireOp",EDGE,"E144");var subQ14=sQuery(id+"F0.wireOp",EDGE,"E143");var subQ15=sQuery(id+"F0.wireOp",EDGE,"E142");var subQ16=sQuery(id+"F0.wireOp",EDGE,"E141");var subQ17=sQuery(id+"F0.wireOp",EDGE,"E140");var subQ18=sQuery(id+"F0.wireOp",EDGE,"E139");var subQ19=sQuery(id+"F0.wireOp",EDGE,"E138");var subQ20=sQuery(id+"F0.wireOp",EDGE,"E137");var subQ21=sQuery(id+"F0.wireOp",EDGE,"E136");var subQ22=sQuery(id+"F0.wireOp",EDGE,"E135");var subQ23=sQuery(id+"F0.wireOp",EDGE,"E134");var subQ24=sQuery(id+"F0.wireOp",EDGE,"E133");var subQ25=sQuery(id+"F0.wireOp",EDGE,"E132");var subQ26=sQuery(id+"F0.wireOp",EDGE,"E131");var subQ27=sQuery(id+"F0.wireOp",EDGE,"E130");var subQ28=sQuery(id+"F0.wireOp",EDGE,"E129");var subQ29=sQuery(id+"F0.wireOp",EDGE,"E128");var subQ30=sQuery(id+"F0.wireOp",EDGE,"E127");var subQ31=sQuery(id+"F0.wireOp",EDGE,"E126");var subQ32=sQuery(id+"F0.wireOp",EDGE,"E125");var subQ33=sQuery(id+"F0.wireOp",EDGE,"E124");var subQ34=sQuery(id+"F0.wireOp",EDGE,"E123");var subQ35=sQuery(id+"F0.wireOp",EDGE,"E122");var subQ36=sQuery(id+"F0.wireOp",EDGE,"E121");var subQ37=sQuery(id+"F0.wireOp",EDGE,"E120");var subQ38=sQuery(id+"F0.wireOp",EDGE,"E119");var subQ39=sQuery(id+"F0.wireOp",EDGE,"E118");var subQ40=sQuery(id+"F0.wireOp",EDGE,"E117");var subQ41=sQuery(id+"F0.wireOp",EDGE,"E116");var subQ42=sQuery(id+"F0.wireOp",EDGE,"E115");var subQ43=sQuery(id+"F0.wireOp",EDGE,"E114");var subQ44=sQuery(id+"F0.wireOp",EDGE,"E113");var subQ45=sQuery(id+"F0.wireOp",EDGE,"E112");var subQ46=sQuery(id+"F0.wireOp",EDGE,"E111");var subQ47=sQuery(id+"F0.wireOp",EDGE,"E110");var subQ48=sQuery(id+"F0.wireOp",EDGE,"E109");var subQ49=sQuery(id+"F0.wireOp",EDGE,"E108");var subQ50=sQuery(id+"F0.wireOp",EDGE,"E107");var subQ51=sQuery(id+"F0.wireOp",EDGE,"E106");var subQ52=sQuery(id+"F0.wireOp",EDGE,"E105");var subQ53=sQuery(id+"F0.wireOp",EDGE,"E104");var subQ54=sQuery(id+"F0.wireOp",EDGE,"E103");var subQ55=sQuery(id+"F0.wireOp",EDGE,"E102");var subQ56=sQuery(id+"F0.wireOp",EDGE,"E101");var subQ57=sQuery(id+"F0.wireOp",EDGE,"E100");var subQ58=sQuery(id+"F0.wireOp",EDGE,"E99");var subQ59=sQuery(id+"F0.wireOp",EDGE,"E98");var subQ60=sQuery(id+"F0.wireOp",EDGE,"E97");var subQ61=sQuery(id+"F0.wireOp",EDGE,"E96");var subQ62=sQuery(id+"F0.wireOp",EDGE,"E95");var subQ63=sQuery(id+"F0.wireOp",EDGE,"E94");var subQ64=sQuery(id+"F0.wireOp",EDGE,"E93");var subQ65=sQuery(id+"F0.wireOp",EDGE,"E92");var subQ66=sQuery(id+"F0.wireOp",EDGE,"E91");var subQ67=sQuery(id+"F0.wireOp",EDGE,"E90");var subQ68=sQuery(id+"F0.wireOp",EDGE,"E89");var subQ69=sQuery(id+"F0.wireOp",EDGE,"E88");var subQ70=sQuery(id+"F0.wireOp",EDGE,"E87");var subQ71=sQuery(id+"F0.wireOp",EDGE,"E86");var subQ72=sQuery(id+"F0.wireOp",EDGE,"E85");var subQ73=sQuery(id+"F0.wireOp",EDGE,"E84");var subQ74=sQuery(id+"F0.wireOp",EDGE,"E83");var subQ75=sQuery(id+"F0.wireOp",EDGE,"E82");var subQ76=sQuery(id+"F0.wireOp",EDGE,"E81");var subQ77=sQuery(id+"F0.wireOp",EDGE,"E80");var subQ78=sQuery(id+"F0.wireOp",EDGE,"E79");var subQ79=sQuery(id+"F0.wireOp",EDGE,"E78");var subQ80=sQuery(id+"F0.wireOp",EDGE,"E77");var subQ81=sQuery(id+"F0.wireOp",EDGE,"E76");var subQ82=sQuery(id+"F0.wireOp",EDGE,"E75");var subQ83=sQuery(id+"F0.wireOp",EDGE,"E74");var subQ84=sQuery(id+"F0.wireOp",EDGE,"E73");var subQ85=sQuery(id+"F0.wireOp",EDGE,"E72");var subQ86=sQuery(id+"F0.wireOp",EDGE,"E71");var subQ87=sQuery(id+"F0.wireOp",EDGE,"E70");var subQ88=sQuery(id+"F0.wireOp",EDGE,"E69");var subQ89=sQuery(id+"F0.wireOp",EDGE,"E68");var subQ90=sQuery(id+"F0.wireOp",EDGE,"E67");var subQ91=sQuery(id+"F0.wireOp",EDGE,"E66");var subQ92=sQuery(id+"F0.wireOp",EDGE,"E65");var subQ93=sQuery(id+"F0.wireOp",EDGE,"E64");var subQ94=sQuery(id+"F0.wireOp",EDGE,"E63");var subQ95=sQuery(id+"F0.wireOp",EDGE,"E62");var subQ96=sQuery(id+"F0.wireOp",EDGE,"E61");var subQ97=sQuery(id+"F0.wireOp",EDGE,"E60");var subQ98=sQuery(id+"F0.wireOp",EDGE,"E59");var subQ99=sQuery(id+"F0.wireOp",EDGE,"E58");var subQ100=sQuery(id+"F0.wireOp",EDGE,"E57");var subQ101=sQuery(id+"F0.wireOp",EDGE,"E56");var subQ102=sQuery(id+"F0.wireOp",EDGE,"E55");var subQ103=sQuery(id+"F0.wireOp",EDGE,"E54");var subQ104=sQuery(id+"F0.wireOp",EDGE,"E53");var subQ105=sQuery(id+"F0.wireOp",EDGE,"E52");var subQ106=sQuery(id+"F0.wireOp",EDGE,"E51");var subQ107=sQuery(id+"F0.wireOp",EDGE,"E50");var subQ108=sQuery(id+"F0.wireOp",EDGE,"E49");var subQ109=sQuery(id+"F0.wireOp",EDGE,"E48");var subQ110=sQuery(id+"F0.wireOp",EDGE,"E47");var subQ111=sQuery(id+"F0.wireOp",EDGE,"E46");var subQ112=sQuery(id+"F0.wireOp",EDGE,"E45");var subQ113=sQuery(id+"F0.wireOp",EDGE,"E44");var subQ114=sQuery(id+"F0.wireOp",EDGE,"E43");var subQ115=sQuery(id+"F0.wireOp",EDGE,"E42");var subQ116=sQuery(id+"F0.wireOp",EDGE,"E41");var subQ117=sQuery(id+"F0.wireOp",EDGE,"E40");var subQ118=sQuery(id+"F0.wireOp",EDGE,"E39");var subQ119=sQuery(id+"F0.wireOp",EDGE,"E38");var subQ120=sQuery(id+"F0.wireOp",EDGE,"E37");var subQ121=sQuery(id+"F0.wireOp",EDGE,"E36");var subQ122=sQuery(id+"F0.wireOp",EDGE,"E35");var subQ123=sQuery(id+"F0.wireOp",EDGE,"E34");var subQ124=sQuery(id+"F0.wireOp",EDGE,"E33");var subQ125=sQuery(id+"F0.wireOp",EDGE,"E32");var subQ126=sQuery(id+"F0.wireOp",EDGE,"E31");var subQ127=sQuery(id+"F0.wireOp",EDGE,"E30");var subQ128=sQuery(id+"F0.wireOp",EDGE,"E29");var subQ129=sQuery(id+"F0.wireOp",EDGE,"E28");var subQ130=sQuery(id+"F0.wireOp",EDGE,"E27");var subQ131=sQuery(id+"F0.wireOp",EDGE,"E26");var subQ132=sQuery(id+"F0.wireOp",EDGE,"E25");var subQ133=sQuery(id+"F0.wireOp",EDGE,"E24");var subQ134=sQuery(id+"F0.wireOp",EDGE,"E23");var subQ135=sQuery(id+"F0.wireOp",EDGE,"E22");var subQ136=sQuery(id+"F0.wireOp",EDGE,"E21");var subQ137=sQuery(id+"F0.wireOp",EDGE,"E20");var subQ138=sQuery(id+"F0.wireOp",EDGE,"E19");var subQ139=sQuery(id+"F0.wireOp",EDGE,"E18");var subQ140=sQuery(id+"F0.wireOp",EDGE,"E17");var subQ141=sQuery(id+"F0.wireOp",EDGE,"E16");var subQ142=sQuery(id+"F0.wireOp",EDGE,"E15");var subQ143=sQuery(id+"F0.wireOp",EDGE,"E14");var subQ144=sQuery(id+"F0.wireOp",EDGE,"E13");var subQ145=sQuery(id+"F0.wireOp",EDGE,"E12");var subQ146=sQuery(id+"F0.wireOp",EDGE,"E11");var subQ147=sQuery(id+"F0.wireOp",EDGE,"E10");var subQ148=sQuery(id+"F0.wireOp",EDGE,"E9");var subQ149=sQuery(id+"F0.wireOp",EDGE,"E8");var subQ150=sQuery(id+"F0.wireOp",EDGE,"E7");var subQ151=sQuery(id+"F0.wireOp",EDGE,"E6");var subQ152=sQuery(id+"F0.wireOp",EDGE,"E5");var subQ153=sQuery(id+"F0.wireOp",EDGE,"E4");var subQ154=sQuery(id+"F0.wireOp",EDGE,"E3");var subQ155=sQuery(id+"F0.wireOp",EDGE,"E2");var subQ156=sQuery(id+"F0.wireOp",EDGE,"E1");var subQ157=sQuery(id+"F0.wireOp",EDGE,"E0");Q1=makeQuery(id+"F4.boolean.opBoolean","MERGE",FACE,{"derivedFrom":[makeQuery(id+"F1.opExtrude","CAP_FACE",FACE,{"disambiguationData":[OSD([subQ157,subQ156,subQ155,subQ154,subQ153,subQ152,subQ151,subQ150,subQ149,subQ148,subQ147,subQ146,subQ145,subQ144,subQ143,subQ142,subQ141,subQ140,subQ139,subQ138,subQ137,subQ136,subQ135,subQ134,subQ133,subQ132,subQ131,subQ130,subQ129,subQ128,subQ127,subQ126,subQ125,subQ124,subQ123,subQ122,subQ121,subQ120,subQ119,subQ118,subQ117,subQ116,subQ115,subQ114,subQ113,subQ112,subQ111,subQ110,subQ109,subQ108,subQ107,subQ106,subQ105,subQ104,subQ103,subQ102,subQ101,subQ100,subQ99,subQ98,subQ97,subQ96,subQ95,subQ94,subQ93,subQ92,subQ91,subQ90,subQ89,subQ88,subQ87,subQ86,subQ85,subQ84,subQ83,subQ82,subQ81,subQ80,subQ79,subQ78,subQ77,subQ76,subQ75,subQ74,subQ73,subQ72,subQ71,subQ70,subQ69,subQ68,subQ67,subQ66,subQ65,subQ64,subQ63,subQ62,subQ61,subQ60,subQ59,subQ58,subQ57,subQ56,subQ55,subQ54,subQ53,subQ52,subQ51,subQ50,subQ49,subQ48,subQ47,subQ46,subQ45,subQ44,subQ43,subQ42,subQ41,subQ40,subQ39,subQ38,subQ37,subQ36,subQ35,subQ34,subQ33,subQ32,subQ31,subQ30,subQ29,subQ28,subQ27,subQ26,subQ25,subQ24,subQ23,subQ22,subQ21,subQ20,subQ19,subQ18,subQ17,subQ16,subQ15,subQ14,subQ13,subQ12,subQ11,subQ10,subQ9,subQ8,subQ7,subQ6,subQ5,subQ4,subQ3,subQ2,subQ1,subQ0])],"isStart":true}),makeQuery(id+"F4.opExtrude","CAP_FACE",FACE,{"disambiguationData":[OSD([subQ157,subQ156,subQ155,subQ154,subQ153,subQ152,subQ151,subQ150,subQ149,subQ148,subQ147,subQ146,subQ145,subQ144,subQ143,subQ142,subQ141,subQ140,subQ139,subQ138,subQ137,subQ136,subQ135,subQ134,subQ133,subQ132,subQ131,subQ130,subQ129,subQ128,subQ127,subQ126,subQ125,subQ124,subQ123,subQ122,subQ121,subQ120,subQ119,subQ118,subQ117,subQ116,subQ115,subQ114,subQ113,subQ112,subQ111,subQ110,subQ109,subQ108,subQ107,subQ106,subQ105,subQ104,subQ103,subQ102,subQ101,subQ100,subQ99,subQ98,subQ97,subQ96,subQ95,subQ94,subQ93,subQ92,subQ91,subQ90,subQ89,subQ88,subQ87,subQ86,subQ85,subQ84,subQ83,subQ82,subQ81,subQ80,subQ79,subQ78,subQ77,subQ76,subQ75,subQ74,subQ73,subQ72,subQ71,subQ70,subQ69,subQ68,subQ67,subQ66,subQ65,subQ64,subQ63,subQ62,subQ61,subQ60,subQ59,subQ58,subQ57,subQ56,subQ55,subQ54,subQ53,subQ52,subQ51,subQ50,subQ49,subQ48,subQ47,subQ46,subQ45,subQ44,subQ43,subQ42,subQ41,subQ40,subQ39,subQ38,subQ37,subQ36,subQ35,subQ34,subQ33,subQ32,subQ31,subQ30,subQ29,subQ28,subQ27,subQ26,subQ25,subQ24,subQ23,subQ22,subQ21,subQ20,subQ19,subQ18,subQ17,subQ16,subQ15,subQ14,subQ13,subQ12,subQ11,subQ10,subQ9,subQ8,subQ7,subQ6,subQ5,subQ4,subQ3,subQ2,subQ1,subQ0]),OD(0.0)],"isStart":false})]});}
            extrude(context, id + "F6", {"entities" : qUnion([Q0]), "operationType" : NewBodyOperationType.ADD, "endBound" : BoundingType.UP_TO_SURFACE, "oppositeDirection" : true, "depth" : 25 * mm, "endBoundEntityFace" : qUnion([Q1]), "offsetDistance" : 25 * mm});
        }
        {
            var Q0;
            Q0=makeQuery(id+"F4.opExtrude","SWEPT_EDGE",EDGE,{"disambiguationData":[OSD([sQuery(id+"F3.wireOp",EDGE,"E159"),sQuery(id+"F3.wireOp",EDGE,"E160")])]});
            var Q1;
            Q1=makeQuery(id+"F4.opExtrude","SWEPT_EDGE",EDGE,{"disambiguationData":[OSD([sQuery(id+"F3.wireOp",EDGE,"E160"),sQuery(id+"F3.wireOp",EDGE,"E161")])]});
            var Q2;
            Q2=makeQuery(id+"F4.opExtrude","SWEPT_EDGE",EDGE,{"disambiguationData":[OSD([sQuery(id+"F3.wireOp",EDGE,"E164"),sQuery(id+"F3.wireOp",EDGE,"E165")])]});
            var Q3;
            Q3=makeQuery(id+"F4.opExtrude","SWEPT_EDGE",EDGE,{"disambiguationData":[OSD([sQuery(id+"F3.wireOp",EDGE,"E163"),sQuery(id+"F3.wireOp",EDGE,"E164")])]});
            var Q4;
            Q4=makeQuery(id+"F4.opExtrude","SWEPT_EDGE",EDGE,{"disambiguationData":[OSD([sQuery(id+"F3.wireOp",EDGE,"E162"),sQuery(id+"F3.wireOp",EDGE,"E163")])]});
            var Q5;
            Q5=makeQuery(id+"F4.opExtrude","SWEPT_EDGE",EDGE,{"disambiguationData":[OSD([sQuery(id+"F3.wireOp",EDGE,"E161"),sQuery(id+"F3.wireOp",EDGE,"E162")])]});
            var Q6;
            Q6=makeQuery(id+"F4.opExtrude","SWEPT_EDGE",EDGE,{"disambiguationData":[OSD([sQuery(id+"F3.wireOp",EDGE,"E172.1"),sQuery(id+"F3.wireOp",EDGE,"E172.2")])]});
            var Q7;
            Q7=makeQuery(id+"F4.opExtrude","SWEPT_EDGE",EDGE,{"disambiguationData":[OSD([sQuery(id+"F3.wireOp",EDGE,"E172.0"),sQuery(id+"F3.wireOp",EDGE,"E172.1")])]});
            fillet(context, id + "F7", {"entities" : qUnion([Q0, Q1, Q2, Q3, Q4, Q5, Q6, Q7]), "radius" : 5 * mm, "tangentPropagation" : true, "allowEdgeOverflow" : false});
        }
        {
            var Q0;
            Q0=makeQuery(id+"F4.opExtrude","SWEPT_EDGE",EDGE,{"disambiguationData":[OSD([sQuery(id+"F3.wireOp",EDGE,"E169"),sQuery(id+"F3.wireOp",EDGE,"E170")])]});
            var Q1;
            Q1=makeQuery(id+"F4.opExtrude","SWEPT_EDGE",EDGE,{"disambiguationData":[OSD([sQuery(id+"F3.wireOp",EDGE,"E170"),sQuery(id+"F3.wireOp",EDGE,"E171")])]});
            fillet(context, id + "F8", {"entities" : qUnion([Q0, Q1]), "radius" : 15 * mm, "tangentPropagation" : true, "allowEdgeOverflow" : false});
        }
        {
            var Q0;
            Q0=qCreatedBy(makeId("Right.planeOp"),FACE);
            var sketch = newSketch(context, id + "F9", { "sketchPlane" : qUnion([Q0])});
            skLineSegment(sketch, "E179.bottom", {"start": v(-3, 27.24) * mm, "end": v(-1.56, 27.24) * mm});
            skLineSegment(sketch, "E179.top", {"start": v(-3, -86.98) * mm, "end": v(-1.56, -86.98) * mm});
            skLineSegment(sketch, "E179.left", {"start": v(-3, 27.24) * mm, "end": v(-3, -86.98) * mm});
            skLineSegment(sketch, "E179.right", {"start": v(-1.56, 27.24) * mm, "end": v(-1.56, -86.98) * mm});
            skSolve(sketch);
        }
        {
            var Q0;
            Q0 = qSketchRegion(id + "F9", true);
            extrude(context, id + "F10", {"entities" : qUnion([Q0]), "operationType" : NewBodyOperationType.REMOVE, "endBound" : BoundingType.THROUGH_ALL, "oppositeDirection" : true, "depth" : 25 * mm, "offsetDistance" : 25 * mm, "hasSecondDirection" : true, "secondDirectionBound" : SecondDirectionBoundingType.THROUGH_ALL, "secondDirectionOppositeDirection" : false, "secondDirectionDepth" : 25 * mm});
        }
    });
